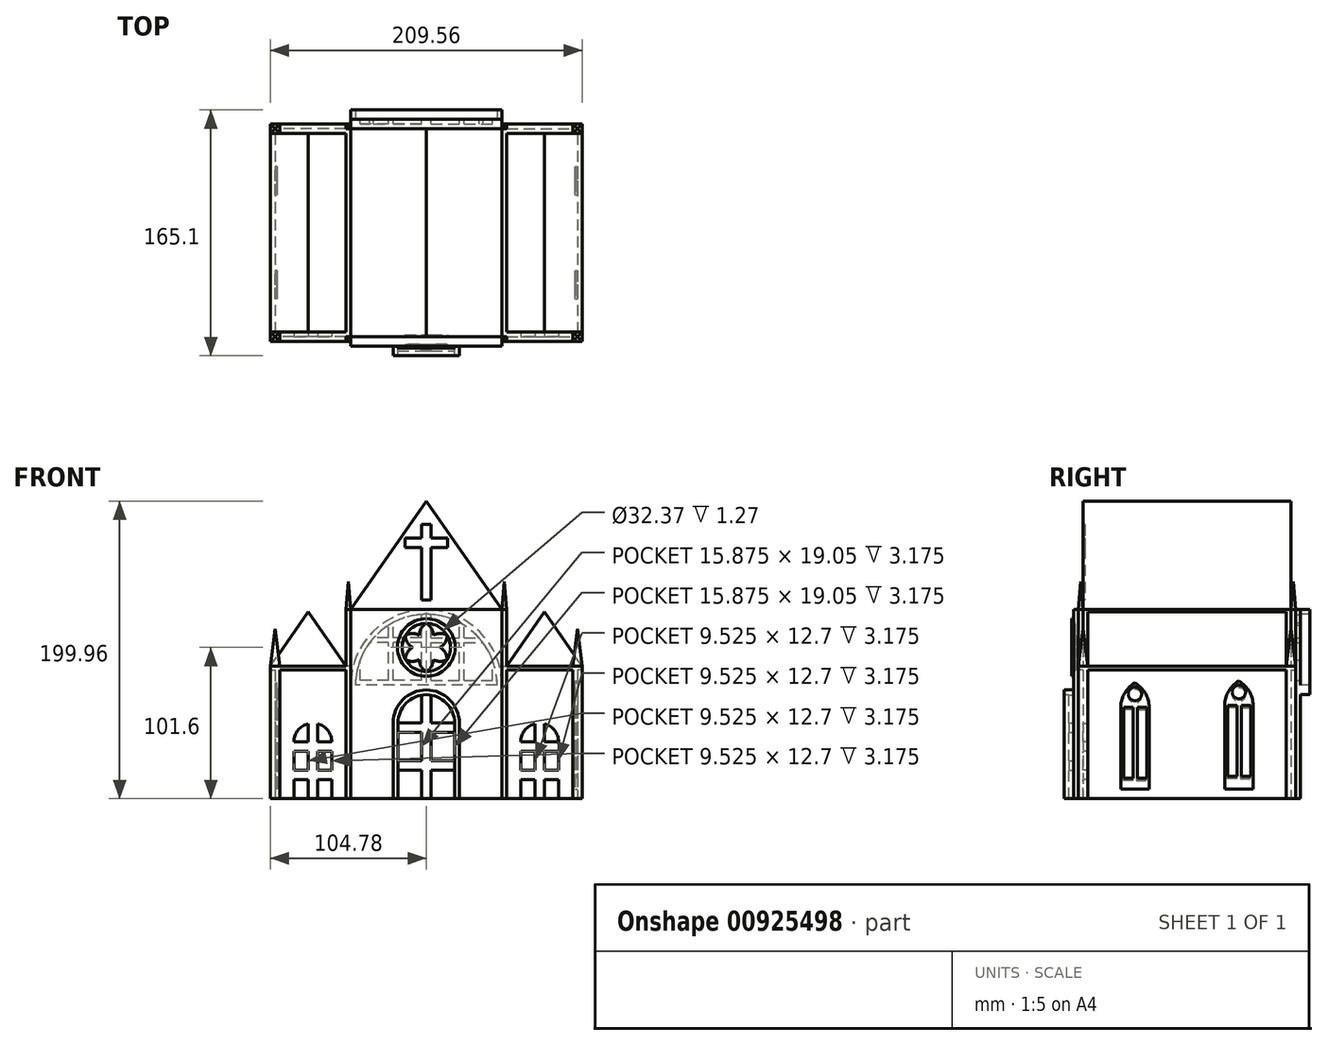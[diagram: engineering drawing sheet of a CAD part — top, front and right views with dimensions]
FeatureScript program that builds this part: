
annotation { "Feature Type Name" : "Feature", "Feature Type Description" : "" }
export const myFeature = defineFeature(function(context is Context, id is Id, definition is map)
    precondition{}
    {
        {
            var Q0;
            Q0=qCreatedBy(makeId("Top.planeOp"),FACE);
            var sketch = newSketch(context, id + "F0", { "sketchPlane" : qUnion([Q0])});
            skLineSegment(sketch, "E0.bottom", {"start": v(-50.8, 76.2) * mm, "end": v(50.8, 76.2) * mm});
            skLineSegment(sketch, "E0.top", {"start": v(-50.8, -76.2) * mm, "end": v(50.8, -76.2) * mm});
            skLineSegment(sketch, "E0.left", {"start": v(-50.8, 76.2) * mm, "end": v(-50.8, 69.85) * mm});
            skLineSegment(sketch, "E0.right", {"start": v(50.8, 76.2) * mm, "end": v(50.8, 69.85) * mm});
            skLineSegment(sketch, "E1.bottom", {"start": v(50.8, 69.85) * mm, "end": v(98.43, 69.85) * mm});
            skLineSegment(sketch, "E1.top", {"start": v(50.8, -69.85) * mm, "end": v(98.43, -69.85) * mm});
            skLineSegment(sketch, "E1.right", {"start": v(101.6, 66.68) * mm, "end": v(101.6, -66.68) * mm});
            skLineSegment(sketch, "E2.bottom", {"start": v(-50.8, 69.85) * mm, "end": v(-98.43, 69.85) * mm});
            skLineSegment(sketch, "E2.top", {"start": v(-50.8, -69.85) * mm, "end": v(-98.42, -69.85) * mm});
            skLineSegment(sketch, "E2.right", {"start": v(-101.6, 66.67) * mm, "end": v(-101.6, -66.68) * mm});
            skLineSegment(sketch, "E3.bottom", {"start": v(50.8, 69.85) * mm, "end": v(53.97, 69.85) * mm});
            skLineSegment(sketch, "E3.top", {"start": v(50.8, 73.03) * mm, "end": v(53.97, 73.03) * mm});
            skLineSegment(sketch, "E3.left", {"start": v(50.8, 69.85) * mm, "end": v(50.8, 73.03) * mm});
            skLineSegment(sketch, "E3.right", {"start": v(53.97, 69.85) * mm, "end": v(53.97, 73.03) * mm});
            skLineSegment(sketch, "E4.bottom", {"start": v(-50.8, 69.85) * mm, "end": v(-53.98, 69.85) * mm});
            skLineSegment(sketch, "E4.top", {"start": v(-50.8, 73.03) * mm, "end": v(-53.98, 73.03) * mm});
            skLineSegment(sketch, "E4.left", {"start": v(-50.8, 69.85) * mm, "end": v(-50.8, 73.03) * mm});
            skLineSegment(sketch, "E4.right", {"start": v(-53.98, 69.85) * mm, "end": v(-53.98, 73.03) * mm});
            skLineSegment(sketch, "E5.bottom", {"start": v(-50.8, -69.85) * mm, "end": v(-53.97, -69.85) * mm});
            skLineSegment(sketch, "E5.top", {"start": v(-50.8, -73.03) * mm, "end": v(-53.97, -73.03) * mm});
            skLineSegment(sketch, "E5.left", {"start": v(-50.8, -69.85) * mm, "end": v(-50.8, -73.03) * mm});
            skLineSegment(sketch, "E5.right", {"start": v(-53.97, -69.85) * mm, "end": v(-53.97, -73.03) * mm});
            skLineSegment(sketch, "E6.bottom", {"start": v(50.8, -69.85) * mm, "end": v(53.98, -69.85) * mm});
            skLineSegment(sketch, "E6.top", {"start": v(50.8, -73.02) * mm, "end": v(53.98, -73.02) * mm});
            skLineSegment(sketch, "E6.left", {"start": v(50.8, -69.85) * mm, "end": v(50.8, -73.02) * mm});
            skLineSegment(sketch, "E6.right", {"start": v(53.98, -69.85) * mm, "end": v(53.98, -73.02) * mm});
            skLineSegment(sketch, "E7.bottom", {"start": v(104.78, 73.03) * mm, "end": v(98.43, 73.03) * mm});
            skLineSegment(sketch, "E7.top", {"start": v(104.78, 66.68) * mm, "end": v(101.6, 66.68) * mm});
            skLineSegment(sketch, "E7.left", {"start": v(104.78, 73.03) * mm, "end": v(104.78, 66.68) * mm});
            skLineSegment(sketch, "E7.right", {"start": v(98.43, 73.03) * mm, "end": v(98.43, 69.85) * mm});
            skPoint(sketch, "E7.middle", {"position": v(101.6, 69.85) * mm});
            skLineSegment(sketch, "E8.bottom", {"start": v(-104.78, 73.02) * mm, "end": v(-98.43, 73.02) * mm});
            skLineSegment(sketch, "E8.top", {"start": v(-104.78, 66.67) * mm, "end": v(-101.6, 66.67) * mm});
            skLineSegment(sketch, "E8.left", {"start": v(-104.78, 73.02) * mm, "end": v(-104.78, 66.67) * mm});
            skLineSegment(sketch, "E8.right", {"start": v(-98.43, 73.02) * mm, "end": v(-98.43, 69.85) * mm});
            skPoint(sketch, "E8.middle", {"position": v(-101.6, 69.85) * mm});
            skLineSegment(sketch, "E9.bottom", {"start": v(-104.77, -73.03) * mm, "end": v(-98.42, -73.03) * mm});
            skLineSegment(sketch, "E9.top", {"start": v(-104.77, -66.68) * mm, "end": v(-101.6, -66.68) * mm});
            skLineSegment(sketch, "E9.left", {"start": v(-104.77, -73.03) * mm, "end": v(-104.77, -66.68) * mm});
            skLineSegment(sketch, "E9.right", {"start": v(-98.42, -73.03) * mm, "end": v(-98.42, -69.85) * mm});
            skPoint(sketch, "E9.middle", {"position": v(-101.6, -69.85) * mm});
            skLineSegment(sketch, "E10.bottom", {"start": v(104.78, -66.68) * mm, "end": v(101.6, -66.68) * mm});
            skLineSegment(sketch, "E10.top", {"start": v(104.78, -73.03) * mm, "end": v(98.43, -73.03) * mm});
            skLineSegment(sketch, "E10.left", {"start": v(104.78, -66.68) * mm, "end": v(104.78, -73.03) * mm});
            skLineSegment(sketch, "E10.right", {"start": v(98.43, -69.85) * mm, "end": v(98.43, -73.03) * mm});
            skPoint(sketch, "E10.middle", {"position": v(101.6, -69.85) * mm});
            skPoint(sketch, "E11.orphan", {"position": v(-98.43, 66.67) * mm});
            skLineSegment(sketch, "E12.trimOffspring", {"start": v(-50.8, -69.85) * mm, "end": v(-50.8, -76.2) * mm});
            skPoint(sketch, "E13.orphan", {"position": v(-98.42, -66.68) * mm});
            skLineSegment(sketch, "E14.trimOffspring", {"start": v(50.8, -69.85) * mm, "end": v(50.8, -76.2) * mm});
            skPoint(sketch, "E15.orphan", {"position": v(98.43, 66.68) * mm});
            skPoint(sketch, "E16.orphan", {"position": v(98.43, -66.68) * mm});
            skLineSegment(sketch, "E17", {"start": v(-50.8, 69.85) * mm, "end": v(-50.8, -69.85) * mm});
            skLineSegment(sketch, "E18", {"start": v(50.8, 69.85) * mm, "end": v(50.8, -69.85) * mm});
            skSolve(sketch);
        }
        {
            var Q0;
            {var subQ2=sQuery(id+"F0.wireOp",EDGE,"E0.bottom");Q0=makeQuery(id+"F0.imprint","IMPRINT",FACE,{"disambiguationData":[TD([[makeQuery(id+"F0.imprint","IMPRINT",EDGE,{"derivedFrom":subQ2}),-1.0]])]});}
            var Q1;
            {var subQ0=sQuery(id+"F0.wireOp",EDGE,"E4.top");Q1=makeQuery(id+"F0.imprint","IMPRINT",FACE,{"disambiguationData":[TD([[makeQuery(id+"F0.imprint","IMPRINT",EDGE,{"derivedFrom":subQ0}),1.0]])]});}
            var Q2;
            {var subQ0=sQuery(id+"F0.wireOp",EDGE,"E3.top");Q2=makeQuery(id+"F0.imprint","IMPRINT",FACE,{"disambiguationData":[TD([[makeQuery(id+"F0.imprint","IMPRINT",EDGE,{"derivedFrom":subQ0}),-1.0]])]});}
            var Q3;
            Q3=makeQuery(id+"F0.imprint","IMPRINT",FACE,{"disambiguationData":[TD([[makeQuery(id+"F0.imprint","IMPRINT",EDGE,{"derivedFrom":sQuery(id+"F0.wireOp",EDGE,"E5.top")}),-1.0]])]});
            var Q4;
            Q4=makeQuery(id+"F0.imprint","IMPRINT",FACE,{"disambiguationData":[TD([[makeQuery(id+"F0.imprint","IMPRINT",EDGE,{"derivedFrom":sQuery(id+"F0.wireOp",EDGE,"E6.top")}),1.0]])]});
            extrude(context, id + "F1", {"entities" : qUnion([Q0, Q1, Q2, Q3, Q4]), "depth" : 127 * mm});
        }
        {
            var Q0;
            {var subQ22=sQuery(id+"F0.wireOp",EDGE,"E3.top");var subQ34=sQuery(id+"F0.wireOp",EDGE,"E4.top");var subQ38=sQuery(id+"F0.wireOp",EDGE,"E0.bottom");Q0=qUnion([makeQuery(id+"F0.imprint","IMPRINT",FACE,{"disambiguationData":[TD([[makeQuery(id+"F0.imprint","IMPRINT",EDGE,{"derivedFrom":sQuery(id+"F0.wireOp",EDGE,"E5.top")}),-1.0]])]}),makeQuery(id+"F0.imprint","IMPRINT",FACE,{"disambiguationData":[TD([[makeQuery(id+"F0.imprint","IMPRINT",EDGE,{"derivedFrom":subQ38}),-1.0]])]}),makeQuery(id+"F0.imprint","IMPRINT",FACE,{"disambiguationData":[TD([[makeQuery(id+"F0.imprint","IMPRINT",EDGE,{"derivedFrom":subQ34}),1.0]])]}),makeQuery(id+"F0.imprint","IMPRINT",FACE,{"disambiguationData":[TD([[makeQuery(id+"F0.imprint","IMPRINT",EDGE,{"derivedFrom":sQuery(id+"F0.wireOp",EDGE,"E1.right")}),-1.0]])]}),makeQuery(id+"F0.imprint","IMPRINT",FACE,{"disambiguationData":[TD([[makeQuery(id+"F0.imprint","IMPRINT",EDGE,{"derivedFrom":subQ22}),-1.0]])]}),makeQuery(id+"F0.imprint","IMPRINT",FACE,{"disambiguationData":[TD([[makeQuery(id+"F0.imprint","IMPRINT",EDGE,{"derivedFrom":sQuery(id+"F0.wireOp",EDGE,"E2.right")}),1.0]])]}),makeQuery(id+"F0.imprint","IMPRINT",FACE,{"disambiguationData":[TD([[makeQuery(id+"F0.imprint","IMPRINT",EDGE,{"derivedFrom":sQuery(id+"F0.wireOp",EDGE,"E6.top")}),1.0]])]})]);}
            extrude(context, id + "F2", {"entities" : qUnion([Q0]), "operationType" : NewBodyOperationType.ADD, "depth" : 88.9 * mm});
        }
        {
            var Q0;
            {var subQ0=sQuery(id+"F0.wireOp",EDGE,"E8.top");var subQ1=sQuery(id+"F0.wireOp",EDGE,"E8.bottom");var subQ2=sQuery(id+"F0.wireOp",EDGE,"E2.top");var subQ3=sQuery(id+"F0.wireOp",EDGE,"E2.bottom");var subQ4=sQuery(id+"F0.wireOp",EDGE,"E4.right");var subQ5=sQuery(id+"F0.wireOp",EDGE,"E8.right");var subQ6=sQuery(id+"F0.wireOp",EDGE,"E2.right");var subQ7=sQuery(id+"F0.wireOp",EDGE,"E5.right");var subQ8=sQuery(id+"F0.wireOp",EDGE,"E9.top");var subQ9=sQuery(id+"F0.wireOp",EDGE,"E8.left");var subQ10=sQuery(id+"F0.wireOp",EDGE,"E9.bottom");var subQ11=sQuery(id+"F0.wireOp",EDGE,"E9.left");var subQ12=sQuery(id+"F0.wireOp",EDGE,"E9.right");Q0=makeQuery(id+"F2.boolean.opBoolean","SPLIT",FACE,{"disambiguationData":[TD([makeQuery(id+"F1.opExtrude","SWEPT_FACE",FACE,{"disambiguationData":[OSD([subQ3])]})])],"derivedFrom":makeQuery(id+"F2.opExtrude","CAP_FACE",FACE,{"disambiguationData":[OSD([sQuery(id+"F0.wireOp",EDGE,"E0.bottom"),sQuery(id+"F0.wireOp",EDGE,"E0.top"),sQuery(id+"F0.wireOp",EDGE,"E0.left"),sQuery(id+"F0.wireOp",EDGE,"E0.right"),sQuery(id+"F0.wireOp",EDGE,"E1.bottom"),sQuery(id+"F0.wireOp",EDGE,"E1.top"),sQuery(id+"F0.wireOp",EDGE,"E1.right"),subQ3,subQ2,subQ6,sQuery(id+"F0.wireOp",EDGE,"E3.top"),sQuery(id+"F0.wireOp",EDGE,"E3.right"),sQuery(id+"F0.wireOp",EDGE,"E4.top"),subQ4,sQuery(id+"F0.wireOp",EDGE,"E5.top"),subQ7,sQuery(id+"F0.wireOp",EDGE,"E6.top"),sQuery(id+"F0.wireOp",EDGE,"E6.right"),sQuery(id+"F0.wireOp",EDGE,"E7.bottom"),sQuery(id+"F0.wireOp",EDGE,"E7.top"),sQuery(id+"F0.wireOp",EDGE,"E7.left"),sQuery(id+"F0.wireOp",EDGE,"E7.right"),subQ1,subQ0,subQ9,subQ5,subQ10,subQ8,subQ11,subQ12,sQuery(id+"F0.wireOp",EDGE,"E10.bottom"),sQuery(id+"F0.wireOp",EDGE,"E10.top"),sQuery(id+"F0.wireOp",EDGE,"E10.left"),sQuery(id+"F0.wireOp",EDGE,"E10.right"),sQuery(id+"F0.wireOp",EDGE,"E12.trimOffspring"),sQuery(id+"F0.wireOp",EDGE,"E14.trimOffspring")])],"isStart":false})});}
            var sketch = newSketch(context, id + "F3", { "sketchPlane" : qUnion([Q0])});
            skLineSegment(sketch, "E19.bottom", {"start": v(-104.78, 73.02) * mm, "end": v(-53.97, 73.02) * mm});
            skLineSegment(sketch, "E19.top", {"start": v(-104.78, -73.03) * mm, "end": v(-53.97, -73.03) * mm});
            skLineSegment(sketch, "E19.left", {"start": v(-104.78, 73.02) * mm, "end": v(-104.78, -73.03) * mm});
            skLineSegment(sketch, "E19.right", {"start": v(-53.97, 73.02) * mm, "end": v(-53.97, -73.03) * mm});
            skSolve(sketch);
        }
        {
            var Q0;
            Q0=qSketchRegion(id+"F3",true);
            extrude(context, id + "F4", {"entities" : qUnion([Q0]), "operationType" : NewBodyOperationType.ADD, "oppositeDirection" : true, "depth" : 2.54 * mm});
        }
        {
            var Q0;
            {var subQ0=sQuery(id+"F0.wireOp",EDGE,"E7.top");var subQ1=sQuery(id+"F0.wireOp",EDGE,"E1.top");var subQ2=sQuery(id+"F0.wireOp",EDGE,"E7.bottom");var subQ3=sQuery(id+"F0.wireOp",EDGE,"E1.bottom");var subQ4=sQuery(id+"F0.wireOp",EDGE,"E1.right");var subQ5=sQuery(id+"F0.wireOp",EDGE,"E6.right");var subQ6=sQuery(id+"F0.wireOp",EDGE,"E10.right");var subQ7=sQuery(id+"F0.wireOp",EDGE,"E3.right");var subQ8=sQuery(id+"F0.wireOp",EDGE,"E7.left");var subQ9=sQuery(id+"F0.wireOp",EDGE,"E7.right");var subQ10=sQuery(id+"F0.wireOp",EDGE,"E10.bottom");var subQ11=sQuery(id+"F0.wireOp",EDGE,"E10.top");var subQ12=sQuery(id+"F0.wireOp",EDGE,"E10.left");Q0=makeQuery(id+"F2.boolean.opBoolean","SPLIT",FACE,{"disambiguationData":[TD([makeQuery(id+"F1.opExtrude","SWEPT_FACE",FACE,{"disambiguationData":[OSD([subQ3])]})])],"derivedFrom":makeQuery(id+"F2.opExtrude","CAP_FACE",FACE,{"disambiguationData":[OSD([sQuery(id+"F0.wireOp",EDGE,"E0.bottom"),sQuery(id+"F0.wireOp",EDGE,"E0.top"),sQuery(id+"F0.wireOp",EDGE,"E0.left"),sQuery(id+"F0.wireOp",EDGE,"E0.right"),subQ3,subQ1,subQ4,sQuery(id+"F0.wireOp",EDGE,"E2.bottom"),sQuery(id+"F0.wireOp",EDGE,"E2.top"),sQuery(id+"F0.wireOp",EDGE,"E2.right"),sQuery(id+"F0.wireOp",EDGE,"E3.top"),subQ7,sQuery(id+"F0.wireOp",EDGE,"E4.top"),sQuery(id+"F0.wireOp",EDGE,"E4.right"),sQuery(id+"F0.wireOp",EDGE,"E5.top"),sQuery(id+"F0.wireOp",EDGE,"E5.right"),sQuery(id+"F0.wireOp",EDGE,"E6.top"),subQ5,subQ2,subQ0,subQ8,subQ9,sQuery(id+"F0.wireOp",EDGE,"E8.bottom"),sQuery(id+"F0.wireOp",EDGE,"E8.top"),sQuery(id+"F0.wireOp",EDGE,"E8.left"),sQuery(id+"F0.wireOp",EDGE,"E8.right"),sQuery(id+"F0.wireOp",EDGE,"E9.bottom"),sQuery(id+"F0.wireOp",EDGE,"E9.top"),sQuery(id+"F0.wireOp",EDGE,"E9.left"),sQuery(id+"F0.wireOp",EDGE,"E9.right"),subQ10,subQ11,subQ12,subQ6,sQuery(id+"F0.wireOp",EDGE,"E12.trimOffspring"),sQuery(id+"F0.wireOp",EDGE,"E14.trimOffspring")])],"isStart":false})});}
            var sketch = newSketch(context, id + "F5", { "sketchPlane" : qUnion([Q0])});
            skLineSegment(sketch, "E20.bottom", {"start": v(104.78, -73.03) * mm, "end": v(53.97, -73.03) * mm});
            skLineSegment(sketch, "E20.top", {"start": v(104.78, 73.03) * mm, "end": v(53.97, 73.03) * mm});
            skLineSegment(sketch, "E20.left", {"start": v(104.78, -73.03) * mm, "end": v(104.78, 73.03) * mm});
            skLineSegment(sketch, "E20.right", {"start": v(53.97, -73.03) * mm, "end": v(53.97, 73.03) * mm});
            skSolve(sketch);
        }
        {
            var Q0;
            {var subQ4=sQuery(id+"F0.wireOp",EDGE,"E1.bottom");var subQ5=makeQuery(id+"F2.opExtrude","CAP_EDGE",EDGE,{"disambiguationData":[OSD([subQ4])],"isStart":false});Q0=makeQuery(id+"F5.imprint","IMPRINT",FACE,{"disambiguationData":[TD([[makeQuery(id+"F5.imprint","IMPRINT",EDGE,{"derivedFrom":subQ5}),-1.0]])]});}
            var Q1;
            Q1=makeQuery(id+"F5.imprint","IMPRINT",FACE,{"disambiguationData":[TD([[makeQuery(id+"F5.imprint","IMPRINT",EDGE,{"derivedFrom":makeQuery(id+"F2.opExtrude","CAP_EDGE",EDGE,{"disambiguationData":[OSD([sQuery(id+"F0.wireOp",EDGE,"E1.right")])],"isStart":false})}),1.0]])]});
            var Q2;
            {var subQ5=sQuery(id+"F0.wireOp",EDGE,"E1.bottom");var subQ6=makeQuery(id+"F2.opExtrude","CAP_EDGE",EDGE,{"disambiguationData":[OSD([subQ5])],"isStart":false});Q2=makeQuery(id+"F5.imprint","IMPRINT",FACE,{"disambiguationData":[TD([[makeQuery(id+"F5.imprint","IMPRINT",EDGE,{"derivedFrom":subQ6}),1.0]])]});}
            var Q3;
            {var subQ5=sQuery(id+"F0.wireOp",EDGE,"E1.top");var subQ6=makeQuery(id+"F2.opExtrude","CAP_EDGE",EDGE,{"disambiguationData":[OSD([subQ5])],"isStart":false});Q3=makeQuery(id+"F5.imprint","IMPRINT",FACE,{"disambiguationData":[TD([[makeQuery(id+"F5.imprint","IMPRINT",EDGE,{"derivedFrom":subQ6}),-1.0]])]});}
            extrude(context, id + "F6", {"entities" : qUnion([Q0, Q1, Q2, Q3]), "operationType" : NewBodyOperationType.ADD, "oppositeDirection" : true, "depth" : 2.54 * mm});
        }
        {
            var Q0;
            Q0=makeQuery(id+"F4.boolean.opBoolean","MERGE",FACE,{"derivedFrom":[makeQuery(id+"F2.opExtrude","SWEPT_FACE",FACE,{"disambiguationData":[OSD([sQuery(id+"F0.wireOp",EDGE,"E9.bottom")])]}),makeQuery(id+"F1.opExtrude","SWEPT_FACE",FACE,{"disambiguationData":[OSD([sQuery(id+"F0.wireOp",EDGE,"E5.top")])]}),makeQuery(id+"F4.opExtrude","SWEPT_FACE",FACE,{"disambiguationData":[OSD([sQuery(id+"F3.wireOp",EDGE,"E19.top")])]})]});
            var sketch = newSketch(context, id + "F7", { "sketchPlane" : qUnion([Q0])});
            skLineSegment(sketch, "E21", {"start": v(-104.77, 88.9) * mm, "end": v(-79.38, 125.38) * mm});
            skPoint(sketch, "E21.endSnap0", {"position": v(-79.37, 88.9) * mm});
            skLineSegment(sketch, "E22", {"start": v(-79.37, 125.38) * mm, "end": v(-53.97, 88.9) * mm});
            skLineSegment(sketch, "E23", {"start": v(-53.97, 88.9) * mm, "end": v(-104.77, 88.9) * mm});
            skSolve(sketch);
        }
        {
            var Q0;
            Q0=makeQuery(id+"F7.imprint","IMPRINT",FACE,{"disambiguationData":[TD([[makeQuery(id+"F7.imprint","IMPRINT",EDGE,{"derivedFrom":sQuery(id+"F7.wireOp",EDGE,"E21")}),-1.0]])]});
            extrude(context, id + "F8", {"entities" : qUnion([Q0]), "oppositeDirection" : true, "depth" : 139.7 * mm});
        }
        {
            var Q0;
            Q0=makeQuery(id+"F6.boolean.opBoolean","MERGE",FACE,{"derivedFrom":[makeQuery(id+"F2.opExtrude","SWEPT_FACE",FACE,{"disambiguationData":[OSD([sQuery(id+"F0.wireOp",EDGE,"E10.top")])]}),makeQuery(id+"F1.opExtrude","SWEPT_FACE",FACE,{"disambiguationData":[OSD([sQuery(id+"F0.wireOp",EDGE,"E6.top")])]}),makeQuery(id+"F6.opExtrude","SWEPT_FACE",FACE,{"disambiguationData":[OSD([sQuery(id+"F5.wireOp",EDGE,"E20.bottom")])]})]});
            var sketch = newSketch(context, id + "F9", { "sketchPlane" : qUnion([Q0])});
            skLineSegment(sketch, "E24", {"start": v(104.78, 88.9) * mm, "end": v(79.38, 125.38) * mm});
            skPoint(sketch, "E24.endSnap0", {"position": v(79.38, 88.9) * mm});
            skLineSegment(sketch, "E25", {"start": v(79.38, 125.38) * mm, "end": v(53.98, 88.9) * mm});
            skLineSegment(sketch, "E26", {"start": v(53.98, 88.9) * mm, "end": v(104.78, 88.9) * mm});
            skSolve(sketch);
        }
        {
            var Q0;
            Q0=makeQuery(id+"F9.imprint","IMPRINT",FACE,{"disambiguationData":[TD([[makeQuery(id+"F9.imprint","IMPRINT",EDGE,{"derivedFrom":sQuery(id+"F9.wireOp",EDGE,"E24")}),1.0]])]});
            extrude(context, id + "F10", {"entities" : qUnion([Q0]), "operationType" : NewBodyOperationType.ADD, "oppositeDirection" : true, "depth" : 139.7 * mm});
        }
        {
            var Q0;
            Q0=makeQuery(id+"F1.opExtrude","SWEPT_FACE",FACE,{"disambiguationData":[OSD([sQuery(id+"F0.wireOp",EDGE,"E0.top")])]});
            var sketch = newSketch(context, id + "F11", { "sketchPlane" : qUnion([Q0])});
            skLineSegment(sketch, "E27", {"start": v(-50.8, 127) * mm, "end": v(0, 199.96) * mm});
            skLineSegment(sketch, "E28", {"start": v(0, 199.96) * mm, "end": v(50.8, 127) * mm});
            skLineSegment(sketch, "E29", {"start": v(50.8, 127) * mm, "end": v(-50.8, 127) * mm});
            skSolve(sketch);
        }
        {
            var Q0;
            Q0=makeQuery(id+"F11.imprint","IMPRINT",FACE,{"disambiguationData":[TD([[makeQuery(id+"F11.imprint","IMPRINT",EDGE,{"derivedFrom":sQuery(id+"F11.wireOp",EDGE,"E27")}),-1.0]])]});
            extrude(context, id + "F12", {"entities" : qUnion([Q0]), "operationType" : NewBodyOperationType.ADD, "oppositeDirection" : true, "depth" : 146.05 * mm});
        }
        {
            var Q0;
            Q0=qSketchRegion(id+"F11",true);
            extrude(context, id + "F13", {"entities" : qUnion([Q0]), "operationType" : NewBodyOperationType.REMOVE, "oppositeDirection" : true, "depth" : 6.35 * mm});
        }
        {
            var Q0;
            Q0=makeQuery(id+"F8.opExtrude","CAP_FACE",FACE,{"disambiguationData":[OSD([sQuery(id+"F7.wireOp",EDGE,"E21"),sQuery(id+"F7.wireOp",EDGE,"E22"),sQuery(id+"F7.wireOp",EDGE,"E23")])],"isStart":true});
            extrude(context, id + "F14", {"entities" : qUnion([Q0]), "operationType" : NewBodyOperationType.REMOVE, "oppositeDirection" : true, "depth" : 6.35 * mm});
        }
        {
            var Q0;
            Q0=qSketchRegion(id+"F9",true);
            extrude(context, id + "F15", {"entities" : qUnion([Q0]), "operationType" : NewBodyOperationType.REMOVE, "oppositeDirection" : true, "depth" : 6.35 * mm});
        }
        {
            var Q0;
            Q0=makeQuery(id+"F4.boolean.opBoolean","MERGE",FACE,{"derivedFrom":[makeQuery(id+"F2.opExtrude","SWEPT_FACE",FACE,{"disambiguationData":[OSD([sQuery(id+"F0.wireOp",EDGE,"E9.bottom")])]}),makeQuery(id+"F1.opExtrude","SWEPT_FACE",FACE,{"disambiguationData":[OSD([sQuery(id+"F0.wireOp",EDGE,"E5.top")])]}),makeQuery(id+"F4.opExtrude","SWEPT_FACE",FACE,{"disambiguationData":[OSD([sQuery(id+"F3.wireOp",EDGE,"E19.top")])]})]});
            var sketch = newSketch(context, id + "F16", { "sketchPlane" : qUnion([Q0])});
            skLineSegment(sketch, "E30", {"start": v(-53.97, 127) * mm, "end": v(-52.39, 145.98) * mm});
            skPoint(sketch, "E30.endSnap0", {"position": v(-52.39, 127) * mm});
            skLineSegment(sketch, "E31", {"start": v(-52.39, 145.98) * mm, "end": v(-50.8, 127) * mm});
            skLineSegment(sketch, "E32", {"start": v(-50.8, 127) * mm, "end": v(-53.97, 127) * mm});
            skSolve(sketch);
        }
        {
            var Q0;
            Q0=makeQuery(id+"F16.imprint","IMPRINT",FACE,{"disambiguationData":[TD([[makeQuery(id+"F16.imprint","IMPRINT",EDGE,{"derivedFrom":sQuery(id+"F16.wireOp",EDGE,"E30")}),-1.0]])]});
            extrude(context, id + "F17", {"entities" : qUnion([Q0]), "operationType" : NewBodyOperationType.ADD, "oppositeDirection" : true, "depth" : 3.17 * mm});
        }
        {
            var Q0;
            Q0=makeQuery(id+"F10.boolean.opBoolean","MERGE",FACE,{"derivedFrom":[makeQuery(id+"F6.boolean.opBoolean","MERGE",FACE,{"derivedFrom":[makeQuery(id+"F2.opExtrude","SWEPT_FACE",FACE,{"disambiguationData":[OSD([sQuery(id+"F0.wireOp",EDGE,"E10.top")])]}),makeQuery(id+"F1.opExtrude","SWEPT_FACE",FACE,{"disambiguationData":[OSD([sQuery(id+"F0.wireOp",EDGE,"E6.top")])]}),makeQuery(id+"F6.opExtrude","SWEPT_FACE",FACE,{"disambiguationData":[OSD([sQuery(id+"F5.wireOp",EDGE,"E20.bottom")])]})]}),makeQuery(id+"F10.opExtrude","CAP_FACE",FACE,{"disambiguationData":[OSD([sQuery(id+"F9.wireOp",EDGE,"E24"),sQuery(id+"F9.wireOp",EDGE,"E25"),sQuery(id+"F9.wireOp",EDGE,"E26")])],"isStart":true})]});
            var sketch = newSketch(context, id + "F18", { "sketchPlane" : qUnion([Q0])});
            skLineSegment(sketch, "E33", {"start": v(50.8, 127) * mm, "end": v(52.39, 145.98) * mm});
            skPoint(sketch, "E33.endSnap0", {"position": v(52.39, 127) * mm});
            skLineSegment(sketch, "E34", {"start": v(52.39, 145.98) * mm, "end": v(53.98, 127) * mm});
            skLineSegment(sketch, "E35", {"start": v(53.98, 127) * mm, "end": v(50.8, 127) * mm});
            skSolve(sketch);
        }
        {
            var Q0;
            Q0=makeQuery(id+"F18.imprint","IMPRINT",FACE,{"disambiguationData":[TD([[makeQuery(id+"F18.imprint","IMPRINT",EDGE,{"derivedFrom":sQuery(id+"F18.wireOp",EDGE,"E33")}),-1.0]])]});
            extrude(context, id + "F19", {"entities" : qUnion([Q0]), "operationType" : NewBodyOperationType.ADD, "oppositeDirection" : true, "depth" : 3.17 * mm});
        }
        {
            var Q0;
            {var subQ5=sQuery(id+"F0.wireOp",EDGE,"E5.right");var subQ11=sQuery(id+"F0.wireOp",EDGE,"E2.top");Q0=makeQuery(id+"F4.boolean.opBoolean","SPLIT",FACE,{"disambiguationData":[TD([makeQuery(id+"F1.opExtrude","SWEPT_FACE",FACE,{"disambiguationData":[OSD([subQ11])]})])],"derivedFrom":makeQuery(id+"F1.opExtrude","SWEPT_FACE",FACE,{"disambiguationData":[OSD([subQ5])]})});}
            var sketch = newSketch(context, id + "F20", { "sketchPlane" : qUnion([Q0])});
            skLineSegment(sketch, "E36", {"start": v(69.85, 127) * mm, "end": v(71.44, 145.98) * mm});
            skPoint(sketch, "E36.endSnap0", {"position": v(71.44, 127) * mm});
            skLineSegment(sketch, "E37", {"start": v(71.44, 145.98) * mm, "end": v(69.85, 145.98) * mm});
            skLineSegment(sketch, "E38", {"start": v(69.85, 145.98) * mm, "end": v(69.85, 127) * mm});
            skLineSegment(sketch, "E39", {"start": v(71.44, 145.98) * mm, "end": v(73.02, 127) * mm});
            skLineSegment(sketch, "E40", {"start": v(73.02, 127) * mm, "end": v(73.02, 145.98) * mm});
            skLineSegment(sketch, "E41", {"start": v(73.02, 145.98) * mm, "end": v(71.44, 145.98) * mm});
            skSolve(sketch);
        }
        {
            var Q0;
            Q0=makeQuery(id+"F20.imprint","IMPRINT",FACE,{"disambiguationData":[TD([[makeQuery(id+"F20.imprint","IMPRINT",EDGE,{"derivedFrom":sQuery(id+"F20.wireOp",EDGE,"E36")}),1.0]])]});
            var Q1;
            Q1=makeQuery(id+"F20.imprint","IMPRINT",FACE,{"disambiguationData":[TD([[makeQuery(id+"F20.imprint","IMPRINT",EDGE,{"derivedFrom":sQuery(id+"F20.wireOp",EDGE,"E39")}),1.0]])]});
            extrude(context, id + "F21", {"entities" : qUnion([Q0, Q1]), "operationType" : NewBodyOperationType.REMOVE, "oppositeDirection" : true, "depth" : 127 * mm});
        }
        {
            var Q0;
            Q0=makeQuery(id+"F4.boolean.opBoolean","MERGE",FACE,{"derivedFrom":[makeQuery(id+"F2.opExtrude","SWEPT_FACE",FACE,{"disambiguationData":[OSD([sQuery(id+"F0.wireOp",EDGE,"E8.bottom")])]}),makeQuery(id+"F1.opExtrude","SWEPT_FACE",FACE,{"disambiguationData":[OSD([sQuery(id+"F0.wireOp",EDGE,"E4.top")])]}),makeQuery(id+"F4.opExtrude","SWEPT_FACE",FACE,{"disambiguationData":[OSD([sQuery(id+"F3.wireOp",EDGE,"E19.bottom")])]})]});
            var sketch = newSketch(context, id + "F22", { "sketchPlane" : qUnion([Q0])});
            skLineSegment(sketch, "E42", {"start": v(53.98, 127) * mm, "end": v(52.39, 145.98) * mm});
            skPoint(sketch, "E42.endSnap0", {"position": v(52.39, 127) * mm});
            skLineSegment(sketch, "E43", {"start": v(52.39, 145.98) * mm, "end": v(50.8, 127) * mm});
            skLineSegment(sketch, "E44", {"start": v(50.8, 127) * mm, "end": v(53.98, 127) * mm});
            skSolve(sketch);
        }
        {
            var Q0;
            Q0=makeQuery(id+"F22.imprint","IMPRINT",FACE,{"disambiguationData":[TD([[makeQuery(id+"F22.imprint","IMPRINT",EDGE,{"derivedFrom":sQuery(id+"F22.wireOp",EDGE,"E42")}),1.0]])]});
            extrude(context, id + "F23", {"entities" : qUnion([Q0]), "operationType" : NewBodyOperationType.ADD, "oppositeDirection" : true, "depth" : 3.17 * mm});
        }
        {
            var Q0;
            Q0=makeQuery(id+"F6.boolean.opBoolean","MERGE",FACE,{"derivedFrom":[makeQuery(id+"F2.opExtrude","SWEPT_FACE",FACE,{"disambiguationData":[OSD([sQuery(id+"F0.wireOp",EDGE,"E7.bottom")])]}),makeQuery(id+"F1.opExtrude","SWEPT_FACE",FACE,{"disambiguationData":[OSD([sQuery(id+"F0.wireOp",EDGE,"E3.top")])]}),makeQuery(id+"F6.opExtrude","SWEPT_FACE",FACE,{"disambiguationData":[OSD([sQuery(id+"F5.wireOp",EDGE,"E20.top")])]})]});
            var sketch = newSketch(context, id + "F24", { "sketchPlane" : qUnion([Q0])});
            skLineSegment(sketch, "E45", {"start": v(-53.97, 127) * mm, "end": v(-52.39, 145.98) * mm});
            skPoint(sketch, "E45.endSnap0", {"position": v(-52.39, 127) * mm});
            skLineSegment(sketch, "E46", {"start": v(-52.39, 145.98) * mm, "end": v(-50.8, 127) * mm});
            skLineSegment(sketch, "E47", {"start": v(-50.8, 127) * mm, "end": v(-53.97, 127) * mm});
            skSolve(sketch);
        }
        {
            var Q0;
            Q0=makeQuery(id+"F24.imprint","IMPRINT",FACE,{"disambiguationData":[TD([[makeQuery(id+"F24.imprint","IMPRINT",EDGE,{"derivedFrom":sQuery(id+"F24.wireOp",EDGE,"E45")}),-1.0]])]});
            extrude(context, id + "F25", {"entities" : qUnion([Q0]), "operationType" : NewBodyOperationType.ADD, "oppositeDirection" : true, "depth" : 3.17 * mm});
        }
        {
            var Q0;
            {var subQ7=sQuery(id+"F0.wireOp",EDGE,"E4.right");var subQ12=sQuery(id+"F0.wireOp",EDGE,"E2.bottom");Q0=makeQuery(id+"F4.boolean.opBoolean","SPLIT",FACE,{"disambiguationData":[TD([makeQuery(id+"F1.opExtrude","SWEPT_FACE",FACE,{"disambiguationData":[OSD([subQ12])]})])],"derivedFrom":makeQuery(id+"F1.opExtrude","SWEPT_FACE",FACE,{"disambiguationData":[OSD([subQ7])]})});}
            var sketch = newSketch(context, id + "F26", { "sketchPlane" : qUnion([Q0])});
            skLineSegment(sketch, "E48", {"start": v(-69.85, 127) * mm, "end": v(-71.44, 145.98) * mm});
            skPoint(sketch, "E48.endSnap0", {"position": v(-71.44, 127) * mm});
            skLineSegment(sketch, "E49", {"start": v(-71.44, 145.98) * mm, "end": v(-69.85, 145.98) * mm});
            skLineSegment(sketch, "E50", {"start": v(-69.85, 145.98) * mm, "end": v(-69.85, 127) * mm});
            skLineSegment(sketch, "E51", {"start": v(-71.44, 145.98) * mm, "end": v(-73.03, 127) * mm});
            skLineSegment(sketch, "E52", {"start": v(-73.03, 127) * mm, "end": v(-73.03, 145.98) * mm});
            skLineSegment(sketch, "E53", {"start": v(-73.03, 145.98) * mm, "end": v(-71.44, 145.98) * mm});
            skSolve(sketch);
        }
        {
            var Q0;
            Q0=makeQuery(id+"F26.imprint","IMPRINT",FACE,{"disambiguationData":[TD([[makeQuery(id+"F26.imprint","IMPRINT",EDGE,{"derivedFrom":sQuery(id+"F26.wireOp",EDGE,"E51")}),-1.0]])]});
            var Q1;
            Q1=makeQuery(id+"F26.imprint","IMPRINT",FACE,{"disambiguationData":[TD([[makeQuery(id+"F26.imprint","IMPRINT",EDGE,{"derivedFrom":sQuery(id+"F26.wireOp",EDGE,"E48")}),-1.0]])]});
            extrude(context, id + "F27", {"entities" : qUnion([Q0, Q1]), "operationType" : NewBodyOperationType.REMOVE, "oppositeDirection" : true, "depth" : 127 * mm});
        }
        {
            var Q0;
            Q0=makeQuery(id+"F17.boolean.opBoolean","MERGE",FACE,{"derivedFrom":[makeQuery(id+"F4.boolean.opBoolean","MERGE",FACE,{"derivedFrom":[makeQuery(id+"F2.opExtrude","SWEPT_FACE",FACE,{"disambiguationData":[OSD([sQuery(id+"F0.wireOp",EDGE,"E9.bottom")])]}),makeQuery(id+"F1.opExtrude","SWEPT_FACE",FACE,{"disambiguationData":[OSD([sQuery(id+"F0.wireOp",EDGE,"E5.top")])]}),makeQuery(id+"F4.opExtrude","SWEPT_FACE",FACE,{"disambiguationData":[OSD([sQuery(id+"F3.wireOp",EDGE,"E19.top")])]})]}),makeQuery(id+"F17.opExtrude","CAP_FACE",FACE,{"disambiguationData":[OSD([sQuery(id+"F16.wireOp",EDGE,"E30"),sQuery(id+"F16.wireOp",EDGE,"E31"),sQuery(id+"F16.wireOp",EDGE,"E32")])],"isStart":true})]});
            var sketch = newSketch(context, id + "F28", { "sketchPlane" : qUnion([Q0])});
            skLineSegment(sketch, "E54", {"start": v(-104.77, 88.9) * mm, "end": v(-98.42, 88.9) * mm});
            skLineSegment(sketch, "E55", {"start": v(-98.42, 88.9) * mm, "end": v(-101.6, 114.1) * mm});
            skPoint(sketch, "E55.endSnap0", {"position": v(-101.6, 88.9) * mm});
            skLineSegment(sketch, "E56", {"start": v(-101.6, 114.1) * mm, "end": v(-104.77, 88.9) * mm});
            skSolve(sketch);
        }
        {
            var Q0;
            Q0=makeQuery(id+"F28.imprint","IMPRINT",FACE,{"disambiguationData":[TD([[makeQuery(id+"F28.imprint","IMPRINT",EDGE,{"derivedFrom":sQuery(id+"F28.wireOp",EDGE,"E54")}),1.0]])]});
            extrude(context, id + "F29", {"entities" : qUnion([Q0]), "oppositeDirection" : true, "depth" : 6.35 * mm});
        }
        {
            var Q0;
            Q0=makeQuery(id+"F4.boolean.opBoolean","MERGE",FACE,{"derivedFrom":[makeQuery(id+"F2.opExtrude","SWEPT_FACE",FACE,{"disambiguationData":[OSD([sQuery(id+"F0.wireOp",EDGE,"E8.left")])]}),makeQuery(id+"F2.opExtrude","SWEPT_FACE",FACE,{"disambiguationData":[OSD([sQuery(id+"F0.wireOp",EDGE,"E9.left")])]}),makeQuery(id+"F4.opExtrude","SWEPT_FACE",FACE,{"disambiguationData":[OSD([sQuery(id+"F3.wireOp",EDGE,"E19.left")])]})]});
            var sketch = newSketch(context, id + "F30", { "sketchPlane" : qUnion([Q0])});
            skLineSegment(sketch, "E57", {"start": v(66.68, 88.9) * mm, "end": v(69.85, 114.1) * mm});
            skPoint(sketch, "E57.endSnap0", {"position": v(69.85, 88.9) * mm});
            skLineSegment(sketch, "E58", {"start": v(69.85, 114.1) * mm, "end": v(73.03, 88.9) * mm});
            skLineSegment(sketch, "E59", {"start": v(66.68, 88.9) * mm, "end": v(66.68, 114.1) * mm});
            skLineSegment(sketch, "E60", {"start": v(66.68, 114.1) * mm, "end": v(69.85, 114.1) * mm});
            skLineSegment(sketch, "E61", {"start": v(73.03, 88.9) * mm, "end": v(73.03, 114.1) * mm});
            skLineSegment(sketch, "E62", {"start": v(73.03, 114.1) * mm, "end": v(69.85, 114.1) * mm});
            skSolve(sketch);
        }
        {
            var Q0;
            Q0=makeQuery(id+"F30.imprint","IMPRINT",FACE,{"disambiguationData":[TD([[makeQuery(id+"F30.imprint","IMPRINT",EDGE,{"derivedFrom":sQuery(id+"F30.wireOp",EDGE,"E58")}),1.0]])]});
            var Q1;
            Q1=makeQuery(id+"F30.imprint","IMPRINT",FACE,{"disambiguationData":[TD([[makeQuery(id+"F30.imprint","IMPRINT",EDGE,{"derivedFrom":sQuery(id+"F30.wireOp",EDGE,"E57")}),1.0]])]});
            extrude(context, id + "F31", {"entities" : qUnion([Q0, Q1]), "operationType" : NewBodyOperationType.REMOVE, "oppositeDirection" : true, "depth" : 25.4 * mm});
        }
        {
            var Q0;
            Q0=makeQuery(id+"F23.boolean.opBoolean","MERGE",FACE,{"derivedFrom":[makeQuery(id+"F4.boolean.opBoolean","MERGE",FACE,{"derivedFrom":[makeQuery(id+"F2.opExtrude","SWEPT_FACE",FACE,{"disambiguationData":[OSD([sQuery(id+"F0.wireOp",EDGE,"E8.bottom")])]}),makeQuery(id+"F1.opExtrude","SWEPT_FACE",FACE,{"disambiguationData":[OSD([sQuery(id+"F0.wireOp",EDGE,"E4.top")])]}),makeQuery(id+"F4.opExtrude","SWEPT_FACE",FACE,{"disambiguationData":[OSD([sQuery(id+"F3.wireOp",EDGE,"E19.bottom")])]})]}),makeQuery(id+"F23.opExtrude","CAP_FACE",FACE,{"disambiguationData":[OSD([sQuery(id+"F22.wireOp",EDGE,"E42"),sQuery(id+"F22.wireOp",EDGE,"E43"),sQuery(id+"F22.wireOp",EDGE,"E44")])],"isStart":true})]});
            var sketch = newSketch(context, id + "F32", { "sketchPlane" : qUnion([Q0])});
            skLineSegment(sketch, "E63", {"start": v(104.78, 88.9) * mm, "end": v(98.43, 88.9) * mm});
            skLineSegment(sketch, "E64", {"start": v(98.43, 88.9) * mm, "end": v(101.6, 114.1) * mm});
            skPoint(sketch, "E64.endSnap0", {"position": v(101.6, 88.9) * mm});
            skLineSegment(sketch, "E65", {"start": v(101.6, 114.1) * mm, "end": v(104.78, 88.9) * mm});
            skSolve(sketch);
        }
        {
            var Q0;
            Q0=makeQuery(id+"F32.imprint","IMPRINT",FACE,{"disambiguationData":[TD([[makeQuery(id+"F32.imprint","IMPRINT",EDGE,{"derivedFrom":sQuery(id+"F32.wireOp",EDGE,"E63")}),-1.0]])]});
            extrude(context, id + "F33", {"entities" : qUnion([Q0]), "oppositeDirection" : true, "depth" : 6.35 * mm});
        }
        {
            var Q0;
            Q0=makeQuery(id+"F4.boolean.opBoolean","MERGE",FACE,{"derivedFrom":[makeQuery(id+"F2.opExtrude","SWEPT_FACE",FACE,{"disambiguationData":[OSD([sQuery(id+"F0.wireOp",EDGE,"E8.left")])]}),makeQuery(id+"F2.opExtrude","SWEPT_FACE",FACE,{"disambiguationData":[OSD([sQuery(id+"F0.wireOp",EDGE,"E9.left")])]}),makeQuery(id+"F4.opExtrude","SWEPT_FACE",FACE,{"disambiguationData":[OSD([sQuery(id+"F3.wireOp",EDGE,"E19.left")])]})]});
            var sketch = newSketch(context, id + "F34", { "sketchPlane" : qUnion([Q0])});
            skLineSegment(sketch, "E66", {"start": v(-66.67, 88.9) * mm, "end": v(-69.85, 114.1) * mm});
            skPoint(sketch, "E66.endSnap0", {"position": v(-69.85, 88.9) * mm});
            skLineSegment(sketch, "E67", {"start": v(-69.85, 114.1) * mm, "end": v(-73.02, 88.9) * mm});
            skLineSegment(sketch, "E68", {"start": v(-73.02, 88.9) * mm, "end": v(-73.02, 114.1) * mm});
            skLineSegment(sketch, "E69", {"start": v(-73.02, 114.1) * mm, "end": v(-69.85, 114.1) * mm});
            skLineSegment(sketch, "E70", {"start": v(-66.67, 88.9) * mm, "end": v(-66.67, 114.1) * mm});
            skLineSegment(sketch, "E71", {"start": v(-66.67, 114.1) * mm, "end": v(-69.85, 114.1) * mm});
            skSolve(sketch);
        }
        {
            var Q0;
            Q0=makeQuery(id+"F34.imprint","IMPRINT",FACE,{"disambiguationData":[TD([[makeQuery(id+"F34.imprint","IMPRINT",EDGE,{"derivedFrom":sQuery(id+"F34.wireOp",EDGE,"E67")}),-1.0]])]});
            var Q1;
            Q1=makeQuery(id+"F34.imprint","IMPRINT",FACE,{"disambiguationData":[TD([[makeQuery(id+"F34.imprint","IMPRINT",EDGE,{"derivedFrom":sQuery(id+"F34.wireOp",EDGE,"E66")}),-1.0]])]});
            extrude(context, id + "F35", {"entities" : qUnion([Q0, Q1]), "operationType" : NewBodyOperationType.REMOVE, "oppositeDirection" : true, "depth" : 14.73 * mm});
        }
        {
            var Q0;
            Q0=makeQuery(id+"F19.boolean.opBoolean","MERGE",FACE,{"derivedFrom":[makeQuery(id+"F10.boolean.opBoolean","MERGE",FACE,{"derivedFrom":[makeQuery(id+"F6.boolean.opBoolean","MERGE",FACE,{"derivedFrom":[makeQuery(id+"F2.opExtrude","SWEPT_FACE",FACE,{"disambiguationData":[OSD([sQuery(id+"F0.wireOp",EDGE,"E10.top")])]}),makeQuery(id+"F1.opExtrude","SWEPT_FACE",FACE,{"disambiguationData":[OSD([sQuery(id+"F0.wireOp",EDGE,"E6.top")])]}),makeQuery(id+"F6.opExtrude","SWEPT_FACE",FACE,{"disambiguationData":[OSD([sQuery(id+"F5.wireOp",EDGE,"E20.bottom")])]})]}),makeQuery(id+"F10.opExtrude","CAP_FACE",FACE,{"disambiguationData":[OSD([sQuery(id+"F9.wireOp",EDGE,"E24"),sQuery(id+"F9.wireOp",EDGE,"E25"),sQuery(id+"F9.wireOp",EDGE,"E26")])],"isStart":true})]}),makeQuery(id+"F19.opExtrude","CAP_FACE",FACE,{"disambiguationData":[OSD([sQuery(id+"F18.wireOp",EDGE,"E33"),sQuery(id+"F18.wireOp",EDGE,"E34"),sQuery(id+"F18.wireOp",EDGE,"E35")])],"isStart":true})]});
            var sketch = newSketch(context, id + "F36", { "sketchPlane" : qUnion([Q0])});
            skLineSegment(sketch, "E72", {"start": v(104.78, 88.9) * mm, "end": v(98.43, 88.9) * mm});
            skLineSegment(sketch, "E73", {"start": v(98.43, 88.9) * mm, "end": v(101.6, 114.1) * mm});
            skPoint(sketch, "E73.endSnap0", {"position": v(101.6, 88.9) * mm});
            skLineSegment(sketch, "E74", {"start": v(101.6, 114.1) * mm, "end": v(104.78, 88.9) * mm});
            skSolve(sketch);
        }
        {
            var Q0;
            Q0=makeQuery(id+"F36.imprint","IMPRINT",FACE,{"disambiguationData":[TD([[makeQuery(id+"F36.imprint","IMPRINT",EDGE,{"derivedFrom":sQuery(id+"F36.wireOp",EDGE,"E72")}),-1.0]])]});
            extrude(context, id + "F37", {"entities" : qUnion([Q0]), "operationType" : NewBodyOperationType.ADD, "oppositeDirection" : true, "depth" : 6.35 * mm});
        }
        {
            var Q0;
            Q0=makeQuery(id+"F6.boolean.opBoolean","MERGE",FACE,{"derivedFrom":[makeQuery(id+"F2.opExtrude","SWEPT_FACE",FACE,{"disambiguationData":[OSD([sQuery(id+"F0.wireOp",EDGE,"E7.left")])]}),makeQuery(id+"F2.opExtrude","SWEPT_FACE",FACE,{"disambiguationData":[OSD([sQuery(id+"F0.wireOp",EDGE,"E10.left")])]}),makeQuery(id+"F6.opExtrude","SWEPT_FACE",FACE,{"disambiguationData":[OSD([sQuery(id+"F5.wireOp",EDGE,"E20.left")])]})]});
            var sketch = newSketch(context, id + "F38", { "sketchPlane" : qUnion([Q0])});
            skLineSegment(sketch, "E75", {"start": v(-73.03, 88.9) * mm, "end": v(-69.85, 114.1) * mm});
            skPoint(sketch, "E75.endSnap0", {"position": v(-69.85, 88.9) * mm});
            skLineSegment(sketch, "E76", {"start": v(-69.85, 114.1) * mm, "end": v(-66.68, 88.9) * mm});
            skLineSegment(sketch, "E77", {"start": v(-66.68, 88.9) * mm, "end": v(-66.68, 114.1) * mm});
            skLineSegment(sketch, "E78", {"start": v(-66.68, 114.1) * mm, "end": v(-69.85, 114.1) * mm});
            skLineSegment(sketch, "E79", {"start": v(-73.03, 88.9) * mm, "end": v(-73.03, 114.1) * mm});
            skLineSegment(sketch, "E80", {"start": v(-73.03, 114.1) * mm, "end": v(-69.85, 114.1) * mm});
            skSolve(sketch);
        }
        {
            var Q0;
            Q0=makeQuery(id+"F38.imprint","IMPRINT",FACE,{"disambiguationData":[TD([[makeQuery(id+"F38.imprint","IMPRINT",EDGE,{"derivedFrom":sQuery(id+"F38.wireOp",EDGE,"E75")}),1.0]])]});
            var Q1;
            Q1=makeQuery(id+"F38.imprint","IMPRINT",FACE,{"disambiguationData":[TD([[makeQuery(id+"F38.imprint","IMPRINT",EDGE,{"derivedFrom":sQuery(id+"F38.wireOp",EDGE,"E76")}),1.0]])]});
            extrude(context, id + "F39", {"entities" : qUnion([Q0, Q1]), "operationType" : NewBodyOperationType.REMOVE, "oppositeDirection" : true, "depth" : 25.4 * mm});
        }
        {
            var Q0;
            Q0=makeQuery(id+"F6.boolean.opBoolean","MERGE",FACE,{"derivedFrom":[makeQuery(id+"F2.opExtrude","SWEPT_FACE",FACE,{"disambiguationData":[OSD([sQuery(id+"F0.wireOp",EDGE,"E7.left")])]}),makeQuery(id+"F2.opExtrude","SWEPT_FACE",FACE,{"disambiguationData":[OSD([sQuery(id+"F0.wireOp",EDGE,"E10.left")])]}),makeQuery(id+"F6.opExtrude","SWEPT_FACE",FACE,{"disambiguationData":[OSD([sQuery(id+"F5.wireOp",EDGE,"E20.left")])]})]});
            var sketch = newSketch(context, id + "F40", { "sketchPlane" : qUnion([Q0])});
            skLineSegment(sketch, "E81", {"start": v(73.02, 88.9) * mm, "end": v(69.85, 114.1) * mm});
            skPoint(sketch, "E81.endSnap0", {"position": v(69.85, 88.9) * mm});
            skLineSegment(sketch, "E82", {"start": v(69.85, 114.1) * mm, "end": v(66.68, 88.9) * mm});
            skLineSegment(sketch, "E83", {"start": v(66.68, 88.9) * mm, "end": v(73.03, 88.9) * mm});
            skSolve(sketch);
        }
        {
            var Q0;
            Q0=makeQuery(id+"F40.imprint","IMPRINT",FACE,{"disambiguationData":[TD([[makeQuery(id+"F40.imprint","IMPRINT",EDGE,{"derivedFrom":sQuery(id+"F40.wireOp",EDGE,"E81")}),1.0]])]});
            extrude(context, id + "F41", {"entities" : qUnion([Q0]), "operationType" : NewBodyOperationType.ADD, "oppositeDirection" : true, "depth" : 6.35 * mm});
        }
        {
            var Q0;
            Q0=makeQuery(id+"F25.boolean.opBoolean","MERGE",FACE,{"derivedFrom":[makeQuery(id+"F6.boolean.opBoolean","MERGE",FACE,{"derivedFrom":[makeQuery(id+"F2.opExtrude","SWEPT_FACE",FACE,{"disambiguationData":[OSD([sQuery(id+"F0.wireOp",EDGE,"E7.bottom")])]}),makeQuery(id+"F1.opExtrude","SWEPT_FACE",FACE,{"disambiguationData":[OSD([sQuery(id+"F0.wireOp",EDGE,"E3.top")])]}),makeQuery(id+"F6.opExtrude","SWEPT_FACE",FACE,{"disambiguationData":[OSD([sQuery(id+"F5.wireOp",EDGE,"E20.top")])]})]}),makeQuery(id+"F25.opExtrude","CAP_FACE",FACE,{"disambiguationData":[OSD([sQuery(id+"F24.wireOp",EDGE,"E45"),sQuery(id+"F24.wireOp",EDGE,"E46"),sQuery(id+"F24.wireOp",EDGE,"E47")])],"isStart":true})]});
            var sketch = newSketch(context, id + "F42", { "sketchPlane" : qUnion([Q0])});
            skLineSegment(sketch, "E84", {"start": v(-98.43, 88.9) * mm, "end": v(-101.6, 114.1) * mm});
            skPoint(sketch, "E84.endSnap0", {"position": v(-101.6, 88.9) * mm});
            skLineSegment(sketch, "E85", {"start": v(-101.6, 114.1) * mm, "end": v(-98.43, 114.1) * mm});
            skLineSegment(sketch, "E86", {"start": v(-98.43, 114.1) * mm, "end": v(-98.43, 88.9) * mm});
            skLineSegment(sketch, "E87", {"start": v(-104.78, 88.9) * mm, "end": v(-101.6, 114.1) * mm});
            skLineSegment(sketch, "E88", {"start": v(-104.78, 114.1) * mm, "end": v(-101.6, 114.1) * mm});
            skLineSegment(sketch, "E89", {"start": v(-104.78, 114.1) * mm, "end": v(-104.78, 88.9) * mm});
            skSolve(sketch);
        }
        {
            var Q0;
            Q0=makeQuery(id+"F42.imprint","IMPRINT",FACE,{"disambiguationData":[TD([[makeQuery(id+"F42.imprint","IMPRINT",EDGE,{"derivedFrom":sQuery(id+"F42.wireOp",EDGE,"E87")}),1.0]])]});
            var Q1;
            Q1=makeQuery(id+"F42.imprint","IMPRINT",FACE,{"disambiguationData":[TD([[makeQuery(id+"F42.imprint","IMPRINT",EDGE,{"derivedFrom":sQuery(id+"F42.wireOp",EDGE,"E84")}),-1.0]])]});
            extrude(context, id + "F43", {"entities" : qUnion([Q0, Q1]), "operationType" : NewBodyOperationType.REMOVE, "oppositeDirection" : true, "depth" : 6.35 * mm});
        }
        {
            var Q0;
            Q0=makeQuery(id+"F12.boolean.opBoolean","MERGE",FACE,{"derivedFrom":[makeQuery(id+"F1.opExtrude","SWEPT_FACE",FACE,{"disambiguationData":[OSD([sQuery(id+"F0.wireOp",EDGE,"E0.top")])]}),makeQuery(id+"F12.opExtrude","CAP_FACE",FACE,{"disambiguationData":[OSD([sQuery(id+"F11.wireOp",EDGE,"E27"),sQuery(id+"F11.wireOp",EDGE,"E28"),sQuery(id+"F11.wireOp",EDGE,"E29")])],"isStart":true})]});
            var sketch = newSketch(context, id + "F44", { "sketchPlane" : qUnion([Q0])});
            skLineSegment(sketch, "E90.bottom", {"start": v(-22.23, 0) * mm, "end": v(22.22, 0) * mm});
            skLineSegment(sketch, "E90.left", {"start": v(-22.23, 0) * mm, "end": v(-22.23, 50.8) * mm});
            skLineSegment(sketch, "E90.right", {"start": v(22.22, 0) * mm, "end": v(22.22, 50.8) * mm});
            skArc(sketch, "E91", {"start": v(22.22, 50.8) * mm, "mid": v(0, 73.02) * mm, "end": v(-22.23, 50.8) * mm});
            skArc(sketch, "E92", {"start": v(19.05, 50.8) * mm, "mid": v(0, 69.85) * mm, "end": v(-19.05, 50.8) * mm});
            skLineSegment(sketch, "E93.top", {"start": v(-19.05, 0) * mm, "end": v(19.05, 0) * mm});
            skLineSegment(sketch, "E93.left", {"start": v(-19.05, 50.8) * mm, "end": v(-19.05, 0) * mm});
            skLineSegment(sketch, "E93.right", {"start": v(19.05, 50.8) * mm, "end": v(19.05, 0) * mm});
            skSolve(sketch);
        }
        {
            var Q0;
            {var subQ1=sQuery(id+"F44.wireOp",EDGE,"E90.left");Q0=makeQuery(id+"F44.imprint","IMPRINT",FACE,{"disambiguationData":[TD([[makeQuery(id+"F44.imprint","IMPRINT",EDGE,{"derivedFrom":subQ1}),-1.0]])]});}
            extrude(context, id + "F45", {"entities" : qUnion([Q0]), "operationType" : NewBodyOperationType.ADD, "depth" : 6.35 * mm});
        }
        {
            var Q0;
            {var subQ1=sQuery(id+"F0.wireOp",EDGE,"E0.top");Q0=makeQuery(id+"F45.boolean.opBoolean","SPLIT",FACE,{"disambiguationData":[TD([makeQuery(id+"F45.opExtrude","SWEPT_FACE",FACE,{"disambiguationData":[OSD([sQuery(id+"F44.wireOp",EDGE,"E92")])]})])],"derivedFrom":makeQuery(id+"F12.boolean.opBoolean","MERGE",FACE,{"derivedFrom":[makeQuery(id+"F1.opExtrude","SWEPT_FACE",FACE,{"disambiguationData":[OSD([subQ1])]}),makeQuery(id+"F12.opExtrude","CAP_FACE",FACE,{"disambiguationData":[OSD([sQuery(id+"F11.wireOp",EDGE,"E27"),sQuery(id+"F11.wireOp",EDGE,"E28"),sQuery(id+"F11.wireOp",EDGE,"E29")])],"isStart":true})]})});}
            var sketch = newSketch(context, id + "F46", { "sketchPlane" : qUnion([Q0])});
            skLineSegment(sketch, "E94.bottom", {"start": v(-3.18, 0) * mm, "end": v(3.17, 0) * mm});
            skLineSegment(sketch, "E94.top", {"start": v(-3.18, 69.85) * mm, "end": v(3.17, 69.85) * mm});
            skLineSegment(sketch, "E94.left", {"start": v(-3.18, 0) * mm, "end": v(-3.18, 19.05) * mm});
            skLineSegment(sketch, "E94.right", {"start": v(3.17, 0) * mm, "end": v(3.17, 19.05) * mm});
            skLineSegment(sketch, "E95.bottom", {"start": v(-19.05, 50.8) * mm, "end": v(-3.18, 50.8) * mm});
            skLineSegment(sketch, "E95.top", {"start": v(-19.05, 44.45) * mm, "end": v(-3.18, 44.45) * mm});
            skLineSegment(sketch, "E95.left", {"start": v(-19.05, 50.8) * mm, "end": v(-19.05, 44.45) * mm});
            skLineSegment(sketch, "E95.right", {"start": v(19.05, 50.8) * mm, "end": v(19.05, 44.45) * mm});
            skLineSegment(sketch, "E96.bottom", {"start": v(-19.05, 25.4) * mm, "end": v(-3.18, 25.4) * mm});
            skLineSegment(sketch, "E96.top", {"start": v(-19.05, 19.05) * mm, "end": v(-3.18, 19.05) * mm});
            skLineSegment(sketch, "E96.left", {"start": v(-19.05, 25.4) * mm, "end": v(-19.05, 19.05) * mm});
            skLineSegment(sketch, "E96.right", {"start": v(19.05, 25.4) * mm, "end": v(19.05, 19.05) * mm});
            skLineSegment(sketch, "E97.trimOffspring", {"start": v(3.17, 50.8) * mm, "end": v(19.05, 50.8) * mm});
            skLineSegment(sketch, "E98.trimOffspring", {"start": v(-3.18, 50.8) * mm, "end": v(-3.18, 69.85) * mm});
            skLineSegment(sketch, "E99.trimOffspring", {"start": v(3.17, 50.8) * mm, "end": v(3.17, 69.85) * mm});
            skLineSegment(sketch, "E100.trimOffspring", {"start": v(3.17, 44.45) * mm, "end": v(19.05, 44.45) * mm});
            skLineSegment(sketch, "E101.trimOffspring", {"start": v(3.17, 25.4) * mm, "end": v(19.05, 25.4) * mm});
            skLineSegment(sketch, "E102.trimOffspring", {"start": v(-3.18, 25.4) * mm, "end": v(-3.18, 44.45) * mm});
            skLineSegment(sketch, "E103.trimOffspring", {"start": v(3.17, 25.4) * mm, "end": v(3.17, 44.45) * mm});
            skLineSegment(sketch, "E104.trimOffspring", {"start": v(3.17, 19.05) * mm, "end": v(19.05, 19.05) * mm});
            skSolve(sketch);
        }
        {
            var Q0;
            Q0=makeQuery(id+"F46.imprint","IMPRINT",FACE,{"disambiguationData":[TD([[makeQuery(id+"F46.imprint","IMPRINT",EDGE,{"derivedFrom":sQuery(id+"F46.wireOp",EDGE,"E94.bottom")}),1.0]])]});
            extrude(context, id + "F47", {"entities" : qUnion([Q0]), "operationType" : NewBodyOperationType.ADD, "depth" : 3.17 * mm});
        }
        {
            var Q0;
            Q0=makeQuery(id+"F13.boolean.opBoolean","COPY",FACE,{"derivedFrom":makeQuery(id+"F13.opExtrude","CAP_FACE",FACE,{"disambiguationData":[OSD([sQuery(id+"F11.wireOp",EDGE,"E27"),sQuery(id+"F11.wireOp",EDGE,"E28"),sQuery(id+"F11.wireOp",EDGE,"E29")])],"isStart":false})});
            var sketch = newSketch(context, id + "F48", { "sketchPlane" : qUnion([Q0])});
            skLineSegment(sketch, "E105.bottom", {"start": v(-3.18, 184.15) * mm, "end": v(3.17, 184.15) * mm});
            skLineSegment(sketch, "E105.top", {"start": v(-3.18, 133.35) * mm, "end": v(3.17, 133.35) * mm});
            skLineSegment(sketch, "E105.left", {"start": v(-3.18, 184.15) * mm, "end": v(-3.18, 133.35) * mm});
            skLineSegment(sketch, "E105.right", {"start": v(3.17, 184.15) * mm, "end": v(3.17, 133.35) * mm});
            skLineSegment(sketch, "E106.bottom", {"start": v(-14.29, 174.95) * mm, "end": v(14.29, 174.95) * mm});
            skLineSegment(sketch, "E106.top", {"start": v(-14.29, 168.6) * mm, "end": v(14.29, 168.6) * mm});
            skLineSegment(sketch, "E106.left", {"start": v(-14.29, 174.95) * mm, "end": v(-14.29, 168.6) * mm});
            skLineSegment(sketch, "E106.right", {"start": v(14.29, 174.95) * mm, "end": v(14.29, 168.6) * mm});
            skSolve(sketch);
        }
        {
            var Q0;
            {var subQ0=sQuery(id+"F48.wireOp",EDGE,"E106.bottom");var subQ1=sQuery(id+"F48.wireOp",EDGE,"E105.left");var subQ2=makeQuery(id+"F48.imprint","INTERSECT",VERTEX,{"derivedFrom":[subQ1,subQ0]});Q0=makeQuery(id+"F48.imprint","IMPRINT",FACE,{"disambiguationData":[TD([[makeQuery(id+"F48.imprint","IMPRINT",EDGE,{"disambiguationData":[TD([[subQ2,-1.0]])],"derivedFrom":subQ1}),1.0]])]});}
            var Q1;
            {var subQ0=sQuery(id+"F48.wireOp",EDGE,"E105.bottom");Q1=makeQuery(id+"F48.imprint","IMPRINT",FACE,{"disambiguationData":[TD([[makeQuery(id+"F48.imprint","IMPRINT",EDGE,{"derivedFrom":subQ0}),-1.0]])]});}
            var Q2;
            {var subQ5=sQuery(id+"F48.wireOp",EDGE,"E106.right");Q2=makeQuery(id+"F48.imprint","IMPRINT",FACE,{"disambiguationData":[TD([[makeQuery(id+"F48.imprint","IMPRINT",EDGE,{"derivedFrom":subQ5}),-1.0]])]});}
            var Q3;
            {var subQ5=sQuery(id+"F48.wireOp",EDGE,"E106.left");Q3=makeQuery(id+"F48.imprint","IMPRINT",FACE,{"disambiguationData":[TD([[makeQuery(id+"F48.imprint","IMPRINT",EDGE,{"derivedFrom":subQ5}),1.0]])]});}
            var Q4;
            {var subQ0=sQuery(id+"F48.wireOp",EDGE,"E105.top");Q4=makeQuery(id+"F48.imprint","IMPRINT",FACE,{"disambiguationData":[TD([[makeQuery(id+"F48.imprint","IMPRINT",EDGE,{"derivedFrom":subQ0}),1.0]])]});}
            extrude(context, id + "F49", {"entities" : qUnion([Q0, Q1, Q2, Q3, Q4]), "operationType" : NewBodyOperationType.REMOVE, "oppositeDirection" : true, "offsetDistance" : 25.4 * mm, "depth" : 1.27 * mm});
        }
        {
            var Q0;
            {var subQ1=sQuery(id+"F0.wireOp",EDGE,"E12.trimOffspring");var subQ18=sQuery(id+"F0.wireOp",EDGE,"E0.top");Q0=makeQuery(id+"F45.boolean.opBoolean","SPLIT",FACE,{"disambiguationData":[TD([makeQuery(id+"F1.opExtrude","SWEPT_FACE",FACE,{"disambiguationData":[OSD([subQ1])]})])],"derivedFrom":makeQuery(id+"F12.boolean.opBoolean","MERGE",FACE,{"derivedFrom":[makeQuery(id+"F1.opExtrude","SWEPT_FACE",FACE,{"disambiguationData":[OSD([subQ18])]}),makeQuery(id+"F12.opExtrude","CAP_FACE",FACE,{"disambiguationData":[OSD([sQuery(id+"F11.wireOp",EDGE,"E27"),sQuery(id+"F11.wireOp",EDGE,"E28"),sQuery(id+"F11.wireOp",EDGE,"E29")])],"isStart":true})]})});}
            var sketch = newSketch(context, id + "F50", { "sketchPlane" : qUnion([Q0])});
            skCircle(sketch, "E107", {"center": v(0, 101.6) * mm, "radius": 19.36 * mm});
            skPoint(sketch, "E107.centerSnap0", {"position": v(0, 73.02) * mm});
            skCircle(sketch, "E108", {"center": v(0, 101.6) * mm, "radius": 16.19 * mm});
            skCircle(sketch, "E109.cCircle", {"center": v(0, 101.6) * mm, "radius": 16.19 * mm, "construction": true});
            skLineSegment(sketch, "E109.0", {"start": v(0, 85.41) * mm, "end": v(-14.02, 93.5) * mm});
            skLineSegment(sketch, "E109.1", {"start": v(-14.02, 93.5) * mm, "end": v(-14.02, 109.7) * mm});
            skLineSegment(sketch, "E109.2", {"start": v(-14.02, 109.7) * mm, "end": v(0, 117.79) * mm});
            skLineSegment(sketch, "E109.3", {"start": v(0, 117.79) * mm, "end": v(14.02, 109.7) * mm});
            skLineSegment(sketch, "E109.4", {"start": v(14.02, 109.7) * mm, "end": v(14.02, 93.5) * mm});
            skLineSegment(sketch, "E109.5", {"start": v(14.02, 93.5) * mm, "end": v(0, 85.41) * mm});
            skArc(sketch, "E110", {"start": v(14.02, 93.5) * mm, "mid": v(9.35, 101.6) * mm, "end": v(0, 101.6) * mm});
            skArc(sketch, "E111", {"start": v(14.02, 109.7) * mm, "mid": v(4.67, 109.7) * mm, "end": v(0, 101.6) * mm});
            skArc(sketch, "E112", {"start": v(0, 117.79) * mm, "mid": v(-4.67, 109.7) * mm, "end": v(0, 101.6) * mm});
            skArc(sketch, "E113", {"start": v(-14.02, 109.7) * mm, "mid": v(-9.35, 101.6) * mm, "end": v(0, 101.6) * mm});
            skArc(sketch, "E114", {"start": v(-14.02, 93.5) * mm, "mid": v(-4.67, 93.5) * mm, "end": v(0, 101.6) * mm});
            skArc(sketch, "E115", {"start": v(0, 85.41) * mm, "mid": v(4.67, 93.5) * mm, "end": v(0, 101.6) * mm});
            skArc(sketch, "E116", {"start": v(0, 101.6) * mm, "mid": v(4.67, 93.5) * mm, "end": v(14.02, 93.5) * mm});
            skArc(sketch, "E117", {"start": v(0, 101.6) * mm, "mid": v(-4.67, 93.5) * mm, "end": v(0, 85.41) * mm});
            skArc(sketch, "E118", {"start": v(0, 101.6) * mm, "mid": v(-9.35, 101.6) * mm, "end": v(-14.02, 93.5) * mm});
            skArc(sketch, "E119", {"start": v(0, 101.6) * mm, "mid": v(-4.67, 109.7) * mm, "end": v(-14.02, 109.7) * mm});
            skArc(sketch, "E120", {"start": v(0, 101.6) * mm, "mid": v(4.67, 109.7) * mm, "end": v(0, 117.79) * mm});
            skArc(sketch, "E121", {"start": v(0, 101.6) * mm, "mid": v(9.35, 101.6) * mm, "end": v(14.02, 109.7) * mm});
            skSolve(sketch);
        }
        {
            var Q0;
            Q0=makeQuery(id+"F50.imprint","IMPRINT",FACE,{"disambiguationData":[TD([[makeQuery(id+"F50.imprint","IMPRINT",EDGE,{"derivedFrom":sQuery(id+"F50.wireOp",EDGE,"E107")}),1.0]])]});
            extrude(context, id + "F51", {"entities" : qUnion([Q0]), "operationType" : NewBodyOperationType.ADD, "offsetDistance" : 25.4 * mm, "depth" : 1.27 * mm});
        }
        {
            var Q0;
            {var subQ1=sQuery(id+"F0.wireOp",EDGE,"E12.trimOffspring");var subQ18=sQuery(id+"F0.wireOp",EDGE,"E0.top");Q0=makeQuery(id+"F51.boolean.opBoolean","SPLIT",FACE,{"disambiguationData":[TD([makeQuery(id+"F51.opExtrude","SWEPT_FACE",FACE,{"disambiguationData":[OSD([sQuery(id+"F50.wireOp",EDGE,"E108")])]})])],"derivedFrom":makeQuery(id+"F45.boolean.opBoolean","SPLIT",FACE,{"disambiguationData":[TD([makeQuery(id+"F1.opExtrude","SWEPT_FACE",FACE,{"disambiguationData":[OSD([subQ1])]})])],"derivedFrom":makeQuery(id+"F12.boolean.opBoolean","MERGE",FACE,{"derivedFrom":[makeQuery(id+"F1.opExtrude","SWEPT_FACE",FACE,{"disambiguationData":[OSD([subQ18])]}),makeQuery(id+"F12.opExtrude","CAP_FACE",FACE,{"disambiguationData":[OSD([sQuery(id+"F11.wireOp",EDGE,"E27"),sQuery(id+"F11.wireOp",EDGE,"E28"),sQuery(id+"F11.wireOp",EDGE,"E29")])],"isStart":true})]})})});}
            var sketch = newSketch(context, id + "F52", { "sketchPlane" : qUnion([Q0])});
            skCircle(sketch, "E122.cCircle", {"center": v(0, 101.6) * mm, "radius": 16.19 * mm, "construction": true});
            skLineSegment(sketch, "E122.0", {"start": v(0, 85.41) * mm, "end": v(-14.02, 93.5) * mm});
            skLineSegment(sketch, "E122.1", {"start": v(-14.02, 93.5) * mm, "end": v(-14.02, 109.7) * mm});
            skLineSegment(sketch, "E122.2", {"start": v(-14.02, 109.7) * mm, "end": v(0, 117.79) * mm});
            skLineSegment(sketch, "E122.3", {"start": v(0, 117.79) * mm, "end": v(14.02, 109.7) * mm});
            skLineSegment(sketch, "E122.4", {"start": v(14.02, 109.7) * mm, "end": v(14.02, 93.5) * mm});
            skLineSegment(sketch, "E122.5", {"start": v(14.02, 93.5) * mm, "end": v(0, 85.41) * mm});
            skArc(sketch, "E123", {"start": v(0, 85.41) * mm, "mid": v(4.67, 93.5) * mm, "end": v(0, 101.6) * mm});
            skArc(sketch, "E124", {"start": v(14.02, 93.5) * mm, "mid": v(9.35, 101.6) * mm, "end": v(0, 101.6) * mm});
            skArc(sketch, "E125", {"start": v(14.02, 109.7) * mm, "mid": v(4.67, 109.7) * mm, "end": v(0, 101.6) * mm});
            skArc(sketch, "E126", {"start": v(0, 117.79) * mm, "mid": v(-4.67, 109.7) * mm, "end": v(0, 101.6) * mm});
            skArc(sketch, "E127", {"start": v(-14.02, 109.7) * mm, "mid": v(-9.35, 101.6) * mm, "end": v(0, 101.6) * mm});
            skArc(sketch, "E128", {"start": v(-14.02, 93.5) * mm, "mid": v(-4.67, 93.5) * mm, "end": v(0, 101.6) * mm});
            skArc(sketch, "E129", {"start": v(0, 101.6) * mm, "mid": v(-4.67, 93.5) * mm, "end": v(0, 85.41) * mm});
            skArc(sketch, "E130", {"start": v(0, 101.6) * mm, "mid": v(-9.35, 101.6) * mm, "end": v(-14.02, 93.5) * mm});
            skArc(sketch, "E131", {"start": v(0, 101.6) * mm, "mid": v(-4.67, 109.7) * mm, "end": v(-14.02, 109.7) * mm});
            skArc(sketch, "E132", {"start": v(0, 101.6) * mm, "mid": v(4.67, 109.7) * mm, "end": v(0, 117.79) * mm});
            skArc(sketch, "E133", {"start": v(0, 101.6) * mm, "mid": v(9.35, 101.6) * mm, "end": v(14.02, 109.7) * mm});
            skArc(sketch, "E134", {"start": v(0, 101.6) * mm, "mid": v(4.67, 93.5) * mm, "end": v(14.02, 93.5) * mm});
            skSolve(sketch);
        }
        {
            var Q0;
            {var subQ1=sQuery(id+"F52.wireOp",EDGE,"E130");var subQ2=sQuery(id+"F52.wireOp",EDGE,"E127");var subQ7=makeQuery(id+"F52.imprint","INTERSECT",VERTEX,{"derivedFrom":[subQ2,subQ1]});Q0=makeQuery(id+"F52.imprint","IMPRINT",FACE,{"disambiguationData":[TD([[makeQuery(id+"F52.imprint","IMPRINT",EDGE,{"disambiguationData":[TD([[subQ7,1.0]])],"derivedFrom":subQ2}),1.0]])]});}
            var Q1;
            {var subQ1=sQuery(id+"F52.wireOp",EDGE,"E131");var subQ2=sQuery(id+"F52.wireOp",EDGE,"E126");var subQ7=makeQuery(id+"F52.imprint","INTERSECT",VERTEX,{"derivedFrom":[subQ2,subQ1]});Q1=makeQuery(id+"F52.imprint","IMPRINT",FACE,{"disambiguationData":[TD([[makeQuery(id+"F52.imprint","IMPRINT",EDGE,{"disambiguationData":[TD([[subQ7,1.0]])],"derivedFrom":subQ2}),1.0]])]});}
            var Q2;
            {var subQ0=sQuery(id+"F52.wireOp",EDGE,"E131");var subQ1=sQuery(id+"F52.wireOp",EDGE,"E126");var subQ3=makeQuery(id+"F52.imprint","INTERSECT",VERTEX,{"derivedFrom":[subQ1,subQ0]});Q2=makeQuery(id+"F52.imprint","IMPRINT",FACE,{"disambiguationData":[TD([[makeQuery(id+"F52.imprint","IMPRINT",EDGE,{"disambiguationData":[TD([[subQ3,-1.0]])],"derivedFrom":subQ1}),1.0]])]});}
            var Q3;
            {var subQ0=sQuery(id+"F52.wireOp",EDGE,"E132");var subQ1=sQuery(id+"F52.wireOp",EDGE,"E125");var subQ3=makeQuery(id+"F52.imprint","INTERSECT",VERTEX,{"derivedFrom":[subQ1,subQ0]});Q3=makeQuery(id+"F52.imprint","IMPRINT",FACE,{"disambiguationData":[TD([[makeQuery(id+"F52.imprint","IMPRINT",EDGE,{"disambiguationData":[TD([[subQ3,-1.0]])],"derivedFrom":subQ1}),1.0]])]});}
            var Q4;
            {var subQ1=sQuery(id+"F52.wireOp",EDGE,"E132");var subQ2=sQuery(id+"F52.wireOp",EDGE,"E125");var subQ6=makeQuery(id+"F52.imprint","INTERSECT",VERTEX,{"derivedFrom":[subQ2,subQ1]});Q4=makeQuery(id+"F52.imprint","IMPRINT",FACE,{"disambiguationData":[TD([[makeQuery(id+"F52.imprint","IMPRINT",EDGE,{"disambiguationData":[TD([[subQ6,1.0]])],"derivedFrom":subQ2}),1.0]])]});}
            var Q5;
            {var subQ0=sQuery(id+"F52.wireOp",EDGE,"E133");var subQ1=sQuery(id+"F52.wireOp",EDGE,"E124");var subQ3=makeQuery(id+"F52.imprint","INTERSECT",VERTEX,{"derivedFrom":[subQ1,subQ0]});Q5=makeQuery(id+"F52.imprint","IMPRINT",FACE,{"disambiguationData":[TD([[makeQuery(id+"F52.imprint","IMPRINT",EDGE,{"disambiguationData":[TD([[subQ3,-1.0]])],"derivedFrom":subQ1}),1.0]])]});}
            var Q6;
            {var subQ1=sQuery(id+"F52.wireOp",EDGE,"E133");var subQ2=sQuery(id+"F52.wireOp",EDGE,"E124");var subQ7=makeQuery(id+"F52.imprint","INTERSECT",VERTEX,{"derivedFrom":[subQ2,subQ1]});Q6=makeQuery(id+"F52.imprint","IMPRINT",FACE,{"disambiguationData":[TD([[makeQuery(id+"F52.imprint","IMPRINT",EDGE,{"disambiguationData":[TD([[subQ7,1.0]])],"derivedFrom":subQ2}),1.0]])]});}
            var Q7;
            {var subQ0=sQuery(id+"F52.wireOp",EDGE,"E134");var subQ1=sQuery(id+"F52.wireOp",EDGE,"E123");var subQ3=makeQuery(id+"F52.imprint","INTERSECT",VERTEX,{"derivedFrom":[subQ1,subQ0]});Q7=makeQuery(id+"F52.imprint","IMPRINT",FACE,{"disambiguationData":[TD([[makeQuery(id+"F52.imprint","IMPRINT",EDGE,{"disambiguationData":[TD([[subQ3,-1.0]])],"derivedFrom":subQ1}),1.0]])]});}
            var Q8;
            {var subQ1=sQuery(id+"F52.wireOp",EDGE,"E123");var subQ3=sQuery(id+"F52.wireOp",EDGE,"E134");var subQ4=makeQuery(id+"F52.imprint","INTERSECT",VERTEX,{"derivedFrom":[subQ1,subQ3]});Q8=makeQuery(id+"F52.imprint","IMPRINT",FACE,{"disambiguationData":[TD([[makeQuery(id+"F52.imprint","IMPRINT",EDGE,{"disambiguationData":[TD([[subQ4,1.0]])],"derivedFrom":subQ1}),1.0]])]});}
            var Q9;
            {var subQ1=sQuery(id+"F52.wireOp",EDGE,"E129");var subQ2=sQuery(id+"F52.wireOp",EDGE,"E128");var subQ7=makeQuery(id+"F52.imprint","INTERSECT",VERTEX,{"derivedFrom":[subQ2,subQ1]});Q9=makeQuery(id+"F52.imprint","IMPRINT",FACE,{"disambiguationData":[TD([[makeQuery(id+"F52.imprint","IMPRINT",EDGE,{"disambiguationData":[TD([[subQ7,1.0]])],"derivedFrom":subQ2}),1.0]])]});}
            var Q10;
            {var subQ0=sQuery(id+"F52.wireOp",EDGE,"E129");var subQ1=sQuery(id+"F52.wireOp",EDGE,"E128");var subQ3=makeQuery(id+"F52.imprint","INTERSECT",VERTEX,{"derivedFrom":[subQ1,subQ0]});Q10=makeQuery(id+"F52.imprint","IMPRINT",FACE,{"disambiguationData":[TD([[makeQuery(id+"F52.imprint","IMPRINT",EDGE,{"disambiguationData":[TD([[subQ3,-1.0]])],"derivedFrom":subQ1}),1.0]])]});}
            var Q11;
            {var subQ0=sQuery(id+"F52.wireOp",EDGE,"E130");var subQ1=sQuery(id+"F52.wireOp",EDGE,"E127");var subQ3=makeQuery(id+"F52.imprint","INTERSECT",VERTEX,{"derivedFrom":[subQ1,subQ0]});Q11=makeQuery(id+"F52.imprint","IMPRINT",FACE,{"disambiguationData":[TD([[makeQuery(id+"F52.imprint","IMPRINT",EDGE,{"disambiguationData":[TD([[subQ3,-1.0]])],"derivedFrom":subQ1}),1.0]])]});}
            extrude(context, id + "F53", {"entities" : qUnion([Q0, Q1, Q2, Q3, Q4, Q5, Q6, Q7, Q8, Q9, Q10, Q11]), "operationType" : NewBodyOperationType.REMOVE, "oppositeDirection" : true, "offsetDistance" : 25.4 * mm, "depth" : 1.27 * mm});
        }
        {
            var Q0;
            Q0=makeQuery(id+"F2.opExtrude","SWEPT_FACE",FACE,{"disambiguationData":[OSD([sQuery(id+"F0.wireOp",EDGE,"E1.top")])]});
            var sketch = newSketch(context, id + "F54", { "sketchPlane" : qUnion([Q0])});
            skLineSegment(sketch, "E135.bottom", {"start": v(63.5, 0) * mm, "end": v(88.9, 0) * mm});
            skLineSegment(sketch, "E135.top", {"start": v(63.5, 38.1) * mm, "end": v(73.03, 38.1) * mm});
            skLineSegment(sketch, "E135.left", {"start": v(63.5, 0) * mm, "end": v(63.5, 12.7) * mm});
            skLineSegment(sketch, "E135.right", {"start": v(88.9, 0) * mm, "end": v(88.9, 12.7) * mm});
            skArc(sketch, "E136", {"start": v(73.03, 50.4) * mm, "mid": v(66.16, 45.88) * mm, "end": v(63.5, 38.1) * mm});
            skLineSegment(sketch, "E137.top", {"start": v(63.5, 31.75) * mm, "end": v(73.03, 31.75) * mm});
            skLineSegment(sketch, "E138.bottom", {"start": v(63.5, 19.05) * mm, "end": v(73.03, 19.05) * mm});
            skLineSegment(sketch, "E138.top", {"start": v(63.5, 12.7) * mm, "end": v(73.03, 12.7) * mm});
            skLineSegment(sketch, "E139.bottom", {"start": v(73.03, 0) * mm, "end": v(79.38, 0) * mm});
            skLineSegment(sketch, "E139.left", {"start": v(73.03, 0) * mm, "end": v(73.03, 12.7) * mm});
            skLineSegment(sketch, "E139.right", {"start": v(79.38, 0) * mm, "end": v(79.38, 12.7) * mm});
            skArc(sketch, "E140.trimOffspring", {"start": v(88.9, 38.1) * mm, "mid": v(86.24, 45.88) * mm, "end": v(79.38, 50.4) * mm});
            skLineSegment(sketch, "E141.trimOffspring", {"start": v(79.38, 31.75) * mm, "end": v(88.9, 31.75) * mm});
            skLineSegment(sketch, "E142.trimOffspring", {"start": v(73.03, 38.1) * mm, "end": v(73.03, 50.4) * mm});
            skLineSegment(sketch, "E143.trimOffspring", {"start": v(79.38, 38.1) * mm, "end": v(79.38, 50.4) * mm});
            skLineSegment(sketch, "E144.trimOffspring", {"start": v(79.38, 38.1) * mm, "end": v(88.9, 38.1) * mm});
            skLineSegment(sketch, "E145.trimOffspring", {"start": v(73.03, 19.05) * mm, "end": v(73.03, 31.75) * mm});
            skLineSegment(sketch, "E146.trimOffspring", {"start": v(63.5, 19.05) * mm, "end": v(63.5, 31.75) * mm});
            skLineSegment(sketch, "E147.trimOffspring", {"start": v(79.38, 19.05) * mm, "end": v(79.38, 31.75) * mm});
            skLineSegment(sketch, "E148.trimOffspring", {"start": v(88.9, 19.05) * mm, "end": v(88.9, 31.75) * mm});
            skLineSegment(sketch, "E149.trimOffspring", {"start": v(79.38, 12.7) * mm, "end": v(88.9, 12.7) * mm});
            skLineSegment(sketch, "E150.trimOffspring", {"start": v(79.38, 19.05) * mm, "end": v(88.9, 19.05) * mm});
            skSolve(sketch);
        }
        {
            var Q0;
            Q0=makeQuery(id+"F54.imprint","IMPRINT",FACE,{"disambiguationData":[TD([[makeQuery(id+"F54.imprint","IMPRINT",EDGE,{"derivedFrom":sQuery(id+"F54.wireOp",EDGE,"E136")}),1.0]])]});
            var Q1;
            Q1=makeQuery(id+"F54.imprint","IMPRINT",FACE,{"disambiguationData":[TD([[makeQuery(id+"F54.imprint","IMPRINT",EDGE,{"derivedFrom":sQuery(id+"F54.wireOp",EDGE,"E140.trimOffspring")}),1.0]])]});
            var Q2;
            Q2=makeQuery(id+"F54.imprint","IMPRINT",FACE,{"disambiguationData":[TD([[makeQuery(id+"F54.imprint","IMPRINT",EDGE,{"derivedFrom":sQuery(id+"F54.wireOp",EDGE,"E137.top")}),-1.0]])]});
            var Q3;
            Q3=makeQuery(id+"F54.imprint","IMPRINT",FACE,{"disambiguationData":[TD([[makeQuery(id+"F54.imprint","IMPRINT",EDGE,{"derivedFrom":sQuery(id+"F54.wireOp",EDGE,"E141.trimOffspring")}),-1.0]])]});
            var Q4;
            {var subQ0=sQuery(id+"F54.wireOp",EDGE,"E135.left");Q4=makeQuery(id+"F54.imprint","IMPRINT",FACE,{"disambiguationData":[TD([[makeQuery(id+"F54.imprint","IMPRINT",EDGE,{"derivedFrom":subQ0}),-1.0]])]});}
            var Q5;
            {var subQ0=sQuery(id+"F54.wireOp",EDGE,"E135.right");Q5=makeQuery(id+"F54.imprint","IMPRINT",FACE,{"disambiguationData":[TD([[makeQuery(id+"F54.imprint","IMPRINT",EDGE,{"derivedFrom":subQ0}),1.0]])]});}
            extrude(context, id + "F55", {"entities" : qUnion([Q0, Q1, Q2, Q3, Q4, Q5]), "operationType" : NewBodyOperationType.REMOVE, "oppositeDirection" : true, "depth" : 3.17 * mm});
        }
        {
            var Q0;
            Q0=makeQuery(id+"F2.opExtrude","SWEPT_FACE",FACE,{"disambiguationData":[OSD([sQuery(id+"F0.wireOp",EDGE,"E2.top")])]});
            var sketch = newSketch(context, id + "F56", { "sketchPlane" : qUnion([Q0])});
            skLineSegment(sketch, "E151.bottom", {"start": v(-88.9, 0) * mm, "end": v(-63.5, 0) * mm});
            skLineSegment(sketch, "E151.top", {"start": v(-88.9, 38.1) * mm, "end": v(-79.37, 38.1) * mm});
            skLineSegment(sketch, "E151.left", {"start": v(-88.9, 0) * mm, "end": v(-88.9, 12.7) * mm});
            skLineSegment(sketch, "E151.right", {"start": v(-63.5, 0) * mm, "end": v(-63.5, 12.7) * mm});
            skArc(sketch, "E152", {"start": v(-79.37, 50.4) * mm, "mid": v(-86.24, 45.88) * mm, "end": v(-88.9, 38.1) * mm});
            skLineSegment(sketch, "E153.top", {"start": v(-88.9, 31.75) * mm, "end": v(-79.38, 31.75) * mm});
            skLineSegment(sketch, "E154.bottom", {"start": v(-88.9, 19.05) * mm, "end": v(-79.38, 19.05) * mm});
            skLineSegment(sketch, "E154.top", {"start": v(-88.9, 12.7) * mm, "end": v(-79.38, 12.7) * mm});
            skLineSegment(sketch, "E155.bottom", {"start": v(-79.38, 0) * mm, "end": v(-73.03, 0) * mm});
            skLineSegment(sketch, "E155.left", {"start": v(-79.38, 0) * mm, "end": v(-79.38, 12.7) * mm});
            skLineSegment(sketch, "E155.right", {"start": v(-73.03, 0) * mm, "end": v(-73.03, 12.7) * mm});
            skArc(sketch, "E156.trimOffspring", {"start": v(-63.5, 38.1) * mm, "mid": v(-66.16, 45.88) * mm, "end": v(-73.02, 50.4) * mm});
            skLineSegment(sketch, "E157.trimOffspring", {"start": v(-73.03, 31.75) * mm, "end": v(-63.5, 31.75) * mm});
            skLineSegment(sketch, "E158.trimOffspring", {"start": v(-79.37, 38.1) * mm, "end": v(-79.37, 50.4) * mm});
            skLineSegment(sketch, "E159.trimOffspring", {"start": v(-73.02, 38.1) * mm, "end": v(-73.02, 50.4) * mm});
            skLineSegment(sketch, "E160.trimOffspring", {"start": v(-73.02, 38.1) * mm, "end": v(-63.5, 38.1) * mm});
            skLineSegment(sketch, "E161.trimOffspring", {"start": v(-79.38, 19.05) * mm, "end": v(-79.38, 31.75) * mm});
            skLineSegment(sketch, "E162.trimOffspring", {"start": v(-88.9, 19.05) * mm, "end": v(-88.9, 31.75) * mm});
            skLineSegment(sketch, "E163.trimOffspring", {"start": v(-73.03, 19.05) * mm, "end": v(-73.03, 31.75) * mm});
            skLineSegment(sketch, "E164.trimOffspring", {"start": v(-63.5, 19.05) * mm, "end": v(-63.5, 31.75) * mm});
            skLineSegment(sketch, "E165.trimOffspring", {"start": v(-73.03, 12.7) * mm, "end": v(-63.5, 12.7) * mm});
            skLineSegment(sketch, "E166.trimOffspring", {"start": v(-73.03, 19.05) * mm, "end": v(-63.5, 19.05) * mm});
            skSolve(sketch);
        }
        {
            var Q0;
            Q0=makeQuery(id+"F56.imprint","IMPRINT",FACE,{"disambiguationData":[TD([[makeQuery(id+"F56.imprint","IMPRINT",EDGE,{"derivedFrom":sQuery(id+"F56.wireOp",EDGE,"E152")}),1.0]])]});
            var Q1;
            Q1=makeQuery(id+"F56.imprint","IMPRINT",FACE,{"disambiguationData":[TD([[makeQuery(id+"F56.imprint","IMPRINT",EDGE,{"derivedFrom":sQuery(id+"F56.wireOp",EDGE,"E156.trimOffspring")}),1.0]])]});
            var Q2;
            Q2=makeQuery(id+"F56.imprint","IMPRINT",FACE,{"disambiguationData":[TD([[makeQuery(id+"F56.imprint","IMPRINT",EDGE,{"derivedFrom":sQuery(id+"F56.wireOp",EDGE,"E153.top")}),-1.0]])]});
            var Q3;
            Q3=makeQuery(id+"F56.imprint","IMPRINT",FACE,{"disambiguationData":[TD([[makeQuery(id+"F56.imprint","IMPRINT",EDGE,{"derivedFrom":sQuery(id+"F56.wireOp",EDGE,"E157.trimOffspring")}),-1.0]])]});
            var Q4;
            {var subQ0=sQuery(id+"F56.wireOp",EDGE,"E151.left");Q4=makeQuery(id+"F56.imprint","IMPRINT",FACE,{"disambiguationData":[TD([[makeQuery(id+"F56.imprint","IMPRINT",EDGE,{"derivedFrom":subQ0}),-1.0]])]});}
            var Q5;
            {var subQ0=sQuery(id+"F56.wireOp",EDGE,"E151.right");Q5=makeQuery(id+"F56.imprint","IMPRINT",FACE,{"disambiguationData":[TD([[makeQuery(id+"F56.imprint","IMPRINT",EDGE,{"derivedFrom":subQ0}),1.0]])]});}
            extrude(context, id + "F57", {"entities" : qUnion([Q0, Q1, Q2, Q3, Q4, Q5]), "operationType" : NewBodyOperationType.REMOVE, "oppositeDirection" : true, "depth" : 3.17 * mm});
        }
        {
            var Q0;
            Q0=makeQuery(id+"F2.opExtrude","SWEPT_FACE",FACE,{"disambiguationData":[OSD([sQuery(id+"F0.wireOp",EDGE,"E1.right")])]});
            var sketch = newSketch(context, id + "F58", { "sketchPlane" : qUnion([Q0])});
            skLineSegment(sketch, "E167.top", {"start": v(-44.45, 6.35) * mm, "end": v(-25.4, 6.35) * mm});
            skLineSegment(sketch, "E167.left", {"start": v(-44.45, 61.32) * mm, "end": v(-44.45, 6.35) * mm});
            skLineSegment(sketch, "E167.right", {"start": v(-25.4, 61.32) * mm, "end": v(-25.4, 6.35) * mm});
            skPoint(sketch, "E168.endSnap0", {"position": v(-34.93, 61.32) * mm});
            skArc(sketch, "E169", {"start": v(-34.93, 77.82) * mm, "mid": v(-41.9, 70.85) * mm, "end": v(-44.45, 61.32) * mm});
            skArc(sketch, "E170", {"start": v(-25.4, 61.32) * mm, "mid": v(-27.95, 70.85) * mm, "end": v(-34.93, 77.82) * mm});
            skLineSegment(sketch, "E171.bottom", {"start": v(-36, 61.32) * mm, "end": v(-42.36, 61.32) * mm});
            skLineSegment(sketch, "E171.top", {"start": v(-36, 13.7) * mm, "end": v(-42.36, 13.7) * mm});
            skLineSegment(sketch, "E171.left", {"start": v(-36, 61.32) * mm, "end": v(-36, 13.7) * mm});
            skLineSegment(sketch, "E171.right", {"start": v(-42.36, 61.32) * mm, "end": v(-42.36, 13.7) * mm});
            skLineSegment(sketch, "E172.bottom", {"start": v(-33.3, 61.32) * mm, "end": v(-26.95, 61.32) * mm});
            skLineSegment(sketch, "E172.top", {"start": v(-33.3, 13.7) * mm, "end": v(-26.95, 13.7) * mm});
            skLineSegment(sketch, "E172.left", {"start": v(-33.3, 61.32) * mm, "end": v(-33.3, 13.7) * mm});
            skLineSegment(sketch, "E172.right", {"start": v(-26.95, 61.32) * mm, "end": v(-26.95, 13.7) * mm});
            skCircle(sketch, "E173", {"center": v(-34.93, 70.39) * mm, "radius": 4.53 * mm});
            skSolve(sketch);
        }
        {
            var Q0;
            Q0=makeQuery(id+"F58.imprint","IMPRINT",FACE,{"disambiguationData":[TD([[makeQuery(id+"F58.imprint","IMPRINT",EDGE,{"derivedFrom":sQuery(id+"F58.wireOp",EDGE,"E167.top")}),-1.0]])]});
            var sketch = newSketch(context, id + "F59", { "sketchPlane" : qUnion([Q0])});
            skLineSegment(sketch, "E174.top", {"start": v(25.4, 6.35) * mm, "end": v(44.45, 6.35) * mm});
            skLineSegment(sketch, "E174.left", {"start": v(25.4, 62.61) * mm, "end": v(25.4, 6.35) * mm});
            skLineSegment(sketch, "E174.right", {"start": v(44.45, 62.61) * mm, "end": v(44.45, 6.35) * mm});
            skPoint(sketch, "E175.endSnap0", {"position": v(34.92, 62.61) * mm});
            skArc(sketch, "E176", {"start": v(34.92, 79.11) * mm, "mid": v(27.95, 72.14) * mm, "end": v(25.4, 62.61) * mm});
            skArc(sketch, "E177", {"start": v(44.45, 62.61) * mm, "mid": v(41.9, 72.14) * mm, "end": v(34.92, 79.11) * mm});
            skLineSegment(sketch, "E178.bottom", {"start": v(33.84, 62.61) * mm, "end": v(27.5, 62.61) * mm});
            skLineSegment(sketch, "E178.top", {"start": v(33.84, 14.99) * mm, "end": v(27.5, 14.99) * mm});
            skLineSegment(sketch, "E178.left", {"start": v(33.84, 62.61) * mm, "end": v(33.84, 14.99) * mm});
            skLineSegment(sketch, "E178.right", {"start": v(27.5, 62.61) * mm, "end": v(27.5, 14.99) * mm});
            skLineSegment(sketch, "E179.bottom", {"start": v(36.55, 62.61) * mm, "end": v(42.9, 62.61) * mm});
            skLineSegment(sketch, "E179.top", {"start": v(36.55, 14.99) * mm, "end": v(42.9, 14.99) * mm});
            skLineSegment(sketch, "E179.left", {"start": v(36.55, 62.61) * mm, "end": v(36.55, 14.99) * mm});
            skLineSegment(sketch, "E179.right", {"start": v(42.9, 62.61) * mm, "end": v(42.9, 14.99) * mm});
            skCircle(sketch, "E180", {"center": v(34.92, 71.68) * mm, "radius": 4.53 * mm});
            skSolve(sketch);
        }
        {
            var Q0;
            Q0=qSketchRegion(id+"F58",true);
            extrude(context, id + "F60", {"entities" : qUnion([Q0]), "operationType" : NewBodyOperationType.REMOVE, "oppositeDirection" : true, "depth" : 1.65 * mm});
        }
        {
            var Q0;
            Q0=makeQuery(id+"F59.imprint","IMPRINT",FACE,{"disambiguationData":[TD([[makeQuery(id+"F59.imprint","IMPRINT",EDGE,{"derivedFrom":sQuery(id+"F59.wireOp",EDGE,"E178.bottom")}),1.0]])]});
            var Q1;
            Q1=makeQuery(id+"F59.imprint","IMPRINT",FACE,{"disambiguationData":[TD([[makeQuery(id+"F59.imprint","IMPRINT",EDGE,{"derivedFrom":sQuery(id+"F59.wireOp",EDGE,"E180")}),1.0]])]});
            var Q2;
            Q2=makeQuery(id+"F59.imprint","IMPRINT",FACE,{"disambiguationData":[TD([[makeQuery(id+"F59.imprint","IMPRINT",EDGE,{"derivedFrom":sQuery(id+"F59.wireOp",EDGE,"E179.bottom")}),-1.0]])]});
            extrude(context, id + "F61", {"entities" : qUnion([Q0, Q1, Q2]), "operationType" : NewBodyOperationType.REMOVE, "oppositeDirection" : true, "offsetDistance" : 25.4 * mm, "depth" : 1.27 * mm});
        }
        {
            var Q0;
            Q0=makeQuery(id+"F59.imprint","IMPRINT",FACE,{"disambiguationData":[TD([[makeQuery(id+"F59.imprint","IMPRINT",EDGE,{"derivedFrom":sQuery(id+"F59.wireOp",EDGE,"E174.top")}),1.0]])]});
            extrude(context, id + "F62", {"entities" : qUnion([Q0]), "operationType" : NewBodyOperationType.REMOVE, "oppositeDirection" : true, "depth" : 1.65 * mm});
        }
        {
            var Q0;
            Q0=makeQuery(id+"F58.imprint","IMPRINT",FACE,{"disambiguationData":[TD([[makeQuery(id+"F58.imprint","IMPRINT",EDGE,{"derivedFrom":sQuery(id+"F58.wireOp",EDGE,"E172.bottom")}),-1.0]])]});
            var Q1;
            Q1=makeQuery(id+"F58.imprint","IMPRINT",FACE,{"disambiguationData":[TD([[makeQuery(id+"F58.imprint","IMPRINT",EDGE,{"derivedFrom":sQuery(id+"F58.wireOp",EDGE,"E171.bottom")}),1.0]])]});
            var Q2;
            Q2=makeQuery(id+"F58.imprint","IMPRINT",FACE,{"disambiguationData":[TD([[makeQuery(id+"F58.imprint","IMPRINT",EDGE,{"derivedFrom":sQuery(id+"F58.wireOp",EDGE,"E173")}),1.0]])]});
            extrude(context, id + "F63", {"entities" : qUnion([Q0, Q1, Q2]), "operationType" : NewBodyOperationType.REMOVE, "oppositeDirection" : true, "offsetDistance" : 25.4 * mm, "depth" : 1.27 * mm});
        }
        {
            var Q0;
            Q0=makeQuery(id+"F2.opExtrude","SWEPT_FACE",FACE,{"disambiguationData":[OSD([sQuery(id+"F0.wireOp",EDGE,"E2.right")])]});
            var sketch = newSketch(context, id + "F64", { "sketchPlane" : qUnion([Q0])});
            skLineSegment(sketch, "E181.top", {"start": v(25.4, 6.35) * mm, "end": v(44.45, 6.35) * mm});
            skLineSegment(sketch, "E181.left", {"start": v(25.4, 59.92) * mm, "end": v(25.4, 6.35) * mm});
            skLineSegment(sketch, "E181.right", {"start": v(44.45, 59.92) * mm, "end": v(44.45, 6.35) * mm});
            skPoint(sketch, "E182.endSnap0", {"position": v(34.92, 59.92) * mm});
            skArc(sketch, "E183", {"start": v(34.92, 76.42) * mm, "mid": v(27.95, 69.44) * mm, "end": v(25.4, 59.92) * mm});
            skArc(sketch, "E184", {"start": v(44.45, 59.92) * mm, "mid": v(41.9, 69.44) * mm, "end": v(34.92, 76.42) * mm});
            skLineSegment(sketch, "E185.bottom", {"start": v(33.84, 59.92) * mm, "end": v(27.5, 59.92) * mm});
            skLineSegment(sketch, "E185.top", {"start": v(33.84, 12.3) * mm, "end": v(27.5, 12.3) * mm});
            skLineSegment(sketch, "E185.left", {"start": v(33.84, 59.92) * mm, "end": v(33.84, 12.3) * mm});
            skLineSegment(sketch, "E185.right", {"start": v(27.5, 59.92) * mm, "end": v(27.5, 12.3) * mm});
            skLineSegment(sketch, "E186.bottom", {"start": v(36.55, 59.92) * mm, "end": v(42.9, 59.92) * mm});
            skLineSegment(sketch, "E186.top", {"start": v(36.55, 12.3) * mm, "end": v(42.9, 12.3) * mm});
            skLineSegment(sketch, "E186.left", {"start": v(36.55, 59.92) * mm, "end": v(36.55, 12.3) * mm});
            skLineSegment(sketch, "E186.right", {"start": v(42.9, 59.92) * mm, "end": v(42.9, 12.3) * mm});
            skCircle(sketch, "E187", {"center": v(34.92, 68.99) * mm, "radius": 4.53 * mm});
            skSolve(sketch);
        }
        {
            var Q0;
            Q0=makeQuery(id+"F64.imprint","IMPRINT",FACE,{"disambiguationData":[TD([[makeQuery(id+"F64.imprint","IMPRINT",EDGE,{"derivedFrom":sQuery(id+"F64.wireOp",EDGE,"E181.top")}),-1.0]])]});
            var sketch = newSketch(context, id + "F65", { "sketchPlane" : qUnion([Q0])});
            skLineSegment(sketch, "E188.top", {"start": v(-44.45, 6.35) * mm, "end": v(-25.4, 6.35) * mm});
            skLineSegment(sketch, "E188.left", {"start": v(-44.45, 60.95) * mm, "end": v(-44.45, 6.35) * mm});
            skLineSegment(sketch, "E188.right", {"start": v(-25.4, 60.95) * mm, "end": v(-25.4, 6.35) * mm});
            skPoint(sketch, "E189.endSnap0", {"position": v(-34.93, 60.95) * mm});
            skArc(sketch, "E190", {"start": v(-34.93, 77.45) * mm, "mid": v(-41.9, 70.48) * mm, "end": v(-44.45, 60.95) * mm});
            skArc(sketch, "E191", {"start": v(-25.4, 60.95) * mm, "mid": v(-27.95, 70.48) * mm, "end": v(-34.93, 77.45) * mm});
            skLineSegment(sketch, "E192.bottom", {"start": v(-36, 60.95) * mm, "end": v(-42.36, 60.95) * mm});
            skLineSegment(sketch, "E192.top", {"start": v(-36, 13.33) * mm, "end": v(-42.36, 13.33) * mm});
            skLineSegment(sketch, "E192.left", {"start": v(-36, 60.95) * mm, "end": v(-36, 13.33) * mm});
            skLineSegment(sketch, "E192.right", {"start": v(-42.36, 60.95) * mm, "end": v(-42.36, 13.33) * mm});
            skLineSegment(sketch, "E193.bottom", {"start": v(-33.3, 60.95) * mm, "end": v(-26.95, 60.95) * mm});
            skLineSegment(sketch, "E193.top", {"start": v(-33.3, 13.33) * mm, "end": v(-26.95, 13.33) * mm});
            skLineSegment(sketch, "E193.left", {"start": v(-33.3, 60.95) * mm, "end": v(-33.3, 13.33) * mm});
            skLineSegment(sketch, "E193.right", {"start": v(-26.95, 60.95) * mm, "end": v(-26.95, 13.33) * mm});
            skCircle(sketch, "E194", {"center": v(-34.93, 70.02) * mm, "radius": 4.53 * mm});
            skSolve(sketch);
        }
        {
            var Q0;
            Q0=makeQuery(id+"F64.imprint","IMPRINT",FACE,{"disambiguationData":[TD([[makeQuery(id+"F64.imprint","IMPRINT",EDGE,{"derivedFrom":sQuery(id+"F64.wireOp",EDGE,"E185.bottom")}),1.0]])]});
            var Q1;
            Q1=makeQuery(id+"F64.imprint","IMPRINT",FACE,{"disambiguationData":[TD([[makeQuery(id+"F64.imprint","IMPRINT",EDGE,{"derivedFrom":sQuery(id+"F64.wireOp",EDGE,"E186.bottom")}),-1.0]])]});
            var Q2;
            Q2=makeQuery(id+"F64.imprint","IMPRINT",FACE,{"disambiguationData":[TD([[makeQuery(id+"F64.imprint","IMPRINT",EDGE,{"derivedFrom":sQuery(id+"F64.wireOp",EDGE,"E187")}),1.0]])]});
            extrude(context, id + "F66", {"entities" : qUnion([Q0, Q1, Q2]), "operationType" : NewBodyOperationType.REMOVE, "oppositeDirection" : true, "offsetDistance" : 25.4 * mm, "depth" : 1.27 * mm});
        }
        {
            var Q0;
            Q0=makeQuery(id+"F64.imprint","IMPRINT",FACE,{"disambiguationData":[TD([[makeQuery(id+"F64.imprint","IMPRINT",EDGE,{"derivedFrom":sQuery(id+"F64.wireOp",EDGE,"E181.top")}),1.0]])]});
            extrude(context, id + "F67", {"entities" : qUnion([Q0]), "operationType" : NewBodyOperationType.REMOVE, "oppositeDirection" : true, "depth" : 1.42 * mm});
        }
        {
            var Q0;
            Q0=makeQuery(id+"F65.imprint","IMPRINT",FACE,{"disambiguationData":[TD([[makeQuery(id+"F65.imprint","IMPRINT",EDGE,{"derivedFrom":sQuery(id+"F65.wireOp",EDGE,"E194")}),1.0]])]});
            var Q1;
            Q1=makeQuery(id+"F65.imprint","IMPRINT",FACE,{"disambiguationData":[TD([[makeQuery(id+"F65.imprint","IMPRINT",EDGE,{"derivedFrom":sQuery(id+"F65.wireOp",EDGE,"E192.bottom")}),1.0]])]});
            var Q2;
            Q2=makeQuery(id+"F65.imprint","IMPRINT",FACE,{"disambiguationData":[TD([[makeQuery(id+"F65.imprint","IMPRINT",EDGE,{"derivedFrom":sQuery(id+"F65.wireOp",EDGE,"E193.bottom")}),-1.0]])]});
            extrude(context, id + "F68", {"entities" : qUnion([Q0, Q1, Q2]), "operationType" : NewBodyOperationType.REMOVE, "oppositeDirection" : true, "offsetDistance" : 25.4 * mm, "depth" : 1.27 * mm});
        }
        {
            var Q0;
            Q0=makeQuery(id+"F65.imprint","IMPRINT",FACE,{"disambiguationData":[TD([[makeQuery(id+"F65.imprint","IMPRINT",EDGE,{"derivedFrom":sQuery(id+"F65.wireOp",EDGE,"E188.top")}),1.0]])]});
            extrude(context, id + "F69", {"entities" : qUnion([Q0]), "operationType" : NewBodyOperationType.REMOVE, "oppositeDirection" : true, "depth" : 1.42 * mm});
        }
        {
            var Q0;
            Q0=makeQuery(id+"F1.opExtrude","SWEPT_FACE",FACE,{"disambiguationData":[OSD([sQuery(id+"F0.wireOp",EDGE,"E0.bottom")])]});
            var sketch = newSketch(context, id + "F70", { "sketchPlane" : qUnion([Q0])});
            skArc(sketch, "E195", {"start": v(50.8, 76.2) * mm, "mid": v(0, 127) * mm, "end": v(-50.8, 76.2) * mm});
            skLineSegment(sketch, "E196.top", {"start": v(-47.63, 76.2) * mm, "end": v(47.63, 76.2) * mm});
            skArc(sketch, "E197", {"start": v(47.63, 76.2) * mm, "mid": v(0, 123.83) * mm, "end": v(-47.63, 76.2) * mm});
            skLineSegment(sketch, "E198.top", {"start": v(0, 76.2) * mm, "end": v(47.63, 76.2) * mm});
            skLineSegment(sketch, "E199.bottom", {"start": v(0, 76.2) * mm, "end": v(-47.63, 76.2) * mm});
            skLineSegment(sketch, "E200.bottom", {"start": v(3.18, 79.38) * mm, "end": v(22.23, 79.38) * mm});
            skLineSegment(sketch, "E200.top", {"start": v(3.17, 104.78) * mm, "end": v(22.22, 104.78) * mm});
            skLineSegment(sketch, "E200.left", {"start": v(3.18, 79.38) * mm, "end": v(3.17, 104.78) * mm});
            skLineSegment(sketch, "E200.right", {"start": v(22.23, 79.38) * mm, "end": v(22.22, 104.78) * mm});
            skLineSegment(sketch, "E201.bottom", {"start": v(3.17, 107.95) * mm, "end": v(22.23, 107.95) * mm});
            skLineSegment(sketch, "E201.left", {"start": v(3.17, 107.95) * mm, "end": v(3.17, 123.72) * mm});
            skLineSegment(sketch, "E201.right", {"start": v(22.22, 107.95) * mm, "end": v(22.22, 118.32) * mm});
            skLineSegment(sketch, "E202.bottom", {"start": v(25.4, 79.38) * mm, "end": v(44.45, 79.38) * mm});
            skLineSegment(sketch, "E202.top", {"start": v(25.4, 104.78) * mm, "end": v(38.1, 104.78) * mm});
            skLineSegment(sketch, "E202.left", {"start": v(25.4, 79.38) * mm, "end": v(25.4, 104.78) * mm});
            skLineSegment(sketch, "E202.right", {"start": v(44.45, 79.38) * mm, "end": v(44.45, 93.3) * mm});
            skLineSegment(sketch, "E203.bottom", {"start": v(25.4, 107.95) * mm, "end": v(35.5, 107.95) * mm});
            skLineSegment(sketch, "E203.left", {"start": v(25.4, 107.95) * mm, "end": v(25.4, 116.49) * mm});
            skLineSegment(sketch, "E204.bottom", {"start": v(-3.17, 79.38) * mm, "end": v(-22.22, 79.38) * mm});
            skLineSegment(sketch, "E204.top", {"start": v(-3.18, 104.78) * mm, "end": v(-22.23, 104.78) * mm});
            skLineSegment(sketch, "E204.left", {"start": v(-3.17, 79.38) * mm, "end": v(-3.18, 104.77) * mm});
            skLineSegment(sketch, "E204.right", {"start": v(-22.22, 79.38) * mm, "end": v(-22.23, 104.77) * mm});
            skLineSegment(sketch, "E205.bottom", {"start": v(-3.18, 107.95) * mm, "end": v(-22.23, 107.95) * mm});
            skLineSegment(sketch, "E205.left", {"start": v(-3.18, 107.95) * mm, "end": v(-3.18, 123.72) * mm});
            skLineSegment(sketch, "E205.right", {"start": v(-22.23, 107.95) * mm, "end": v(-22.23, 118.32) * mm});
            skLineSegment(sketch, "E206.bottom", {"start": v(-25.4, 79.38) * mm, "end": v(-44.45, 79.38) * mm});
            skLineSegment(sketch, "E206.top", {"start": v(-25.4, 104.78) * mm, "end": v(-38.1, 104.78) * mm});
            skLineSegment(sketch, "E206.left", {"start": v(-25.4, 79.38) * mm, "end": v(-25.4, 104.77) * mm});
            skLineSegment(sketch, "E206.right", {"start": v(-44.45, 79.38) * mm, "end": v(-44.45, 93.3) * mm});
            skLineSegment(sketch, "E207.bottom", {"start": v(-25.4, 107.95) * mm, "end": v(-35.5, 107.95) * mm});
            skLineSegment(sketch, "E207.left", {"start": v(-25.4, 107.95) * mm, "end": v(-25.4, 116.49) * mm});
            skPoint(sketch, "E208.orphan", {"position": v(-22.23, 133.35) * mm});
            skPoint(sketch, "E209.orphan", {"position": v(-44.45, 133.35) * mm});
            skPoint(sketch, "E201.top.start.orphan", {"position": v(3.17, 133.35) * mm});
            skPoint(sketch, "E210.orphan", {"position": v(22.22, 133.35) * mm});
            skPoint(sketch, "E203.top.end.orphan", {"position": v(44.45, 133.35) * mm});
            skPoint(sketch, "E211.orphan", {"position": v(-44.45, 104.77) * mm});
            skPoint(sketch, "E198.left.start.orphan", {"position": v(0, 127) * mm});
            skPoint(sketch, "E212.trimOffspring.end.orphan", {"position": v(44.45, 104.78) * mm});
            skLineSegment(sketch, "E213.top", {"start": v(-50.8, 69.85) * mm, "end": v(50.8, 69.85) * mm});
            skLineSegment(sketch, "E213.left", {"start": v(-50.8, 76.2) * mm, "end": v(-50.8, 69.85) * mm});
            skLineSegment(sketch, "E213.right", {"start": v(50.8, 76.2) * mm, "end": v(50.8, 69.85) * mm});
            skSolve(sketch);
        }
        {
            var Q0;
            {var subQ13=sQuery(id+"F70.wireOp",EDGE,"E196.top");Q0=makeQuery(id+"F70.imprint","IMPRINT",FACE,{"disambiguationData":[TD([[makeQuery(id+"F70.imprint","IMPRINT",EDGE,{"derivedFrom":subQ13}),-1.0]])]});}
            extrude(context, id + "F71", {"entities" : qUnion([Q0]), "operationType" : NewBodyOperationType.ADD, "depth" : 6.35 * mm});
        }
        {
            var Q0;
            Q0=makeQuery(id+"F70.imprint","IMPRINT",FACE,{"disambiguationData":[TD([[makeQuery(id+"F70.imprint","IMPRINT",EDGE,{"derivedFrom":sQuery(id+"F70.wireOp",EDGE,"E200.bottom")}),1.0]])]});
            var Q1;
            Q1=makeQuery(id+"F70.imprint","IMPRINT",FACE,{"disambiguationData":[TD([[makeQuery(id+"F70.imprint","IMPRINT",EDGE,{"derivedFrom":sQuery(id+"F70.wireOp",EDGE,"E201.bottom")}),1.0]])]});
            var Q2;
            Q2=makeQuery(id+"F70.imprint","IMPRINT",FACE,{"disambiguationData":[TD([[makeQuery(id+"F70.imprint","IMPRINT",EDGE,{"derivedFrom":sQuery(id+"F70.wireOp",EDGE,"E205.bottom")}),-1.0]])]});
            var Q3;
            {var subQ0=sQuery(id+"F70.wireOp",EDGE,"E207.bottom");Q3=makeQuery(id+"F70.imprint","IMPRINT",FACE,{"disambiguationData":[TD([[makeQuery(id+"F70.imprint","IMPRINT",EDGE,{"derivedFrom":subQ0}),-1.0]])]});}
            var Q4;
            Q4=makeQuery(id+"F70.imprint","IMPRINT",FACE,{"disambiguationData":[TD([[makeQuery(id+"F70.imprint","IMPRINT",EDGE,{"derivedFrom":sQuery(id+"F70.wireOp",EDGE,"E206.bottom")}),-1.0]])]});
            var Q5;
            Q5=makeQuery(id+"F70.imprint","IMPRINT",FACE,{"disambiguationData":[TD([[makeQuery(id+"F70.imprint","IMPRINT",EDGE,{"derivedFrom":sQuery(id+"F70.wireOp",EDGE,"E204.bottom")}),-1.0]])]});
            var Q6;
            {var subQ0=sQuery(id+"F70.wireOp",EDGE,"E203.bottom");Q6=makeQuery(id+"F70.imprint","IMPRINT",FACE,{"disambiguationData":[TD([[makeQuery(id+"F70.imprint","IMPRINT",EDGE,{"derivedFrom":subQ0}),1.0]])]});}
            var Q7;
            Q7=makeQuery(id+"F70.imprint","IMPRINT",FACE,{"disambiguationData":[TD([[makeQuery(id+"F70.imprint","IMPRINT",EDGE,{"derivedFrom":sQuery(id+"F70.wireOp",EDGE,"E202.bottom")}),1.0]])]});
            extrude(context, id + "F72", {"entities" : qUnion([Q0, Q1, Q2, Q3, Q4, Q5, Q6, Q7]), "operationType" : NewBodyOperationType.REMOVE, "oppositeDirection" : true, "depth" : 3.17 * mm});
        }
    });
